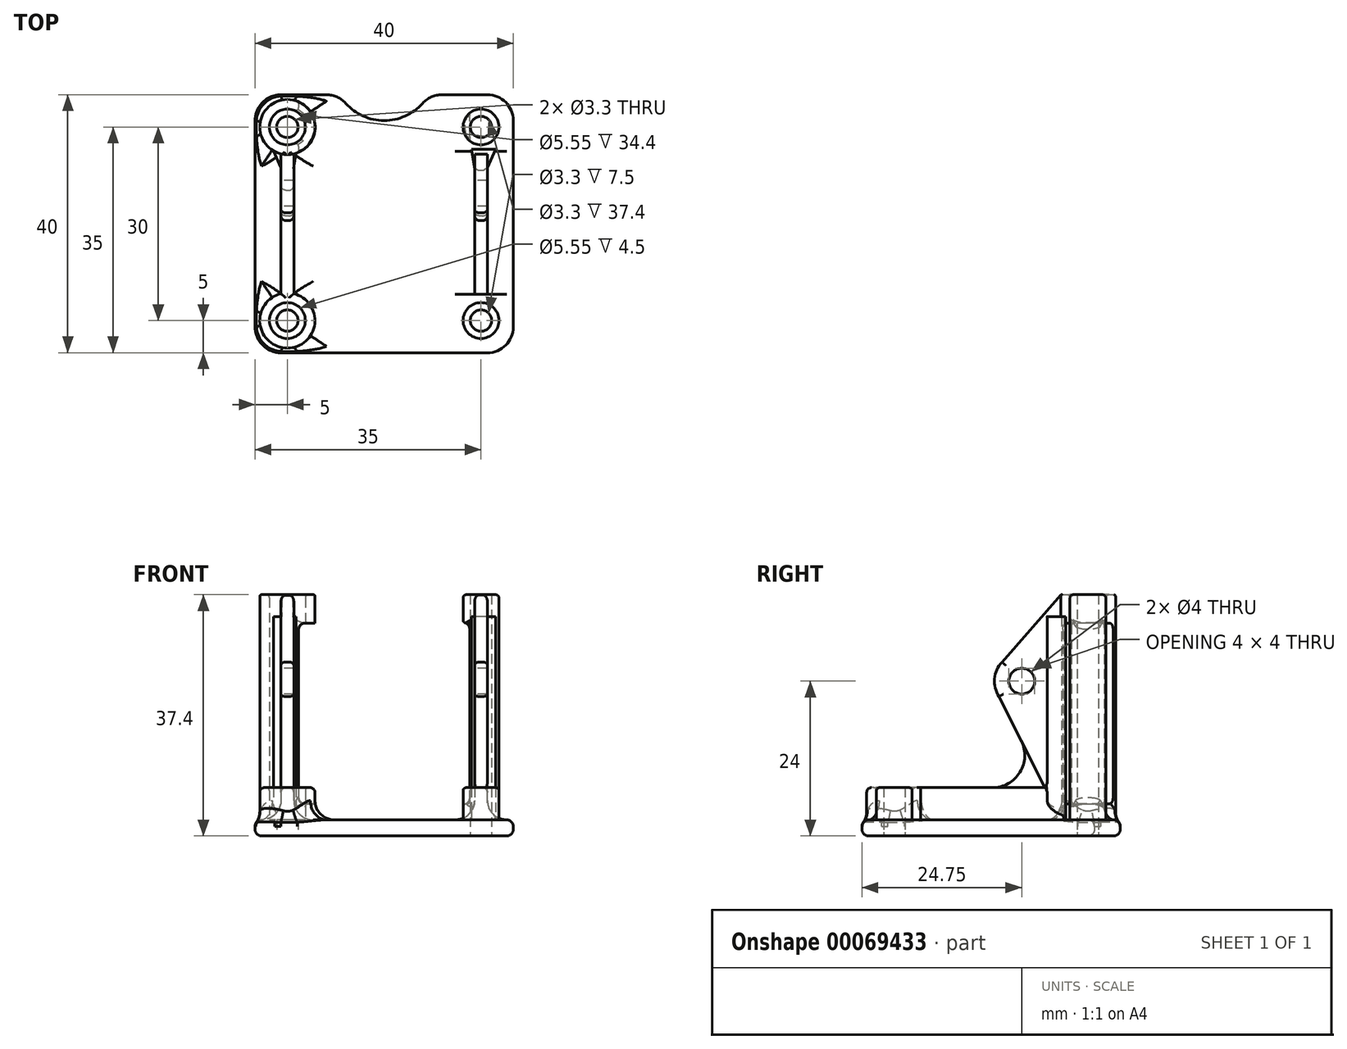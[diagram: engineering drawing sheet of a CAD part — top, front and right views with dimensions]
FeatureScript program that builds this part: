
annotation { "Feature Type Name" : "Feature", "Feature Type Description" : "" }
export const myFeature = defineFeature(function(context is Context, id is Id, definition is map)
    precondition{}
    {
        {
            var Q0;
            Q0=qCreatedBy(makeId("Top.planeOp"),FACE);
            var sketch = newSketch(context, id + "F0", { "sketchPlane" : qUnion([Q0])});
            skLineSegment(sketch, "E0.rect.bottom", {"start": v(20, 20) * mm, "end": v(-20, 20) * mm});
            skLineSegment(sketch, "E0.rect.top", {"start": v(20, -20) * mm, "end": v(-20, -20) * mm});
            skLineSegment(sketch, "E0.rect.left", {"start": v(20, 20) * mm, "end": v(20, -20) * mm});
            skLineSegment(sketch, "E0.rect.right", {"start": v(-20, 20) * mm, "end": v(-20, -20) * mm});
            skPoint(sketch, "E0.rect.middle", {"position": v(0, 0) * mm});
            skCircle(sketch, "E1", {"center": v(-15, 15) * mm, "radius": 1.65 * mm});
            skCircle(sketch, "E2", {"center": v(-15, -15) * mm, "radius": 1.65 * mm});
            skCircle(sketch, "E3.MirrorC", {"center": v(15, 15) * mm, "radius": 1.65 * mm});
            skCircle(sketch, "E4.MirrorC", {"center": v(15, -15) * mm, "radius": 1.65 * mm});
            skCircle(sketch, "E5", {"center": v(0, 24) * mm, "radius": 8 * mm});
            skSolve(sketch);
        }
        {
            var Q0;
            Q0=makeQuery(id+"F0.imprint","IMPRINT",FACE,{"disambiguationData":[TD([[makeQuery(id+"F0.imprint","IMPRINT",EDGE,{"derivedFrom":sQuery(id+"F0.wireOp",EDGE,"E0.rect.top")}),-1.0]])]});
            extrude(context, id + "F1", {"entities" : qUnion([Q0]), "depth" : 2.5 * mm});
        }
        {
            var Q0;
            Q0=makeQuery(id+"F1.opExtrude","CAP_FACE",FACE,{"disambiguationData":[OSD([sQuery(id+"F0.wireOp",EDGE,"E0.rect.bottom"),sQuery(id+"F0.wireOp",EDGE,"E0.rect.top"),sQuery(id+"F0.wireOp",EDGE,"E0.rect.left"),sQuery(id+"F0.wireOp",EDGE,"E0.rect.right"),sQuery(id+"F0.wireOp",EDGE,"E1"),sQuery(id+"F0.wireOp",EDGE,"E2"),sQuery(id+"F0.wireOp",EDGE,"E3.MirrorC"),sQuery(id+"F0.wireOp",EDGE,"E4.MirrorC")])],"isStart":false});
            var sketch = newSketch(context, id + "F2", { "sketchPlane" : qUnion([Q0])});
            skCircle(sketch, "E6", {"center": v(-15, 15) * mm, "radius": 2.77 * mm});
            skCircle(sketch, "E7", {"center": v(-15, 15) * mm, "radius": 4.28 * mm});
            skCircle(sketch, "E8", {"center": v(-15, -15) * mm, "radius": 2.77 * mm});
            skCircle(sketch, "E9", {"center": v(-15, -15) * mm, "radius": 4.28 * mm});
            skCircle(sketch, "E10.MirrorC", {"center": v(15, 15) * mm, "radius": 2.77 * mm});
            skCircle(sketch, "E11.MirrorC", {"center": v(15, 15) * mm, "radius": 4.28 * mm});
            skCircle(sketch, "E12.MirrorC", {"center": v(15, -15) * mm, "radius": 2.77 * mm});
            skCircle(sketch, "E13.MirrorC", {"center": v(15, -15) * mm, "radius": 4.28 * mm});
            skSolve(sketch);
        }
        {
            var Q0;
            Q0=makeQuery(id+"F2.imprint","IMPRINT",FACE,{"disambiguationData":[TD([[makeQuery(id+"F2.imprint","IMPRINT",EDGE,{"derivedFrom":sQuery(id+"F2.wireOp",EDGE,"E8")}),-1.0]])]});
            var Q1;
            Q1=makeQuery(id+"F2.imprint","IMPRINT",FACE,{"disambiguationData":[TD([[makeQuery(id+"F2.imprint","IMPRINT",EDGE,{"derivedFrom":sQuery(id+"F2.wireOp",EDGE,"E12.MirrorC")}),1.0]])]});
            extrude(context, id + "F3", {"entities" : qUnion([Q0, Q1]), "operationType" : NewBodyOperationType.ADD, "depth" : 5 * mm});
        }
        {
            var Q0;
            Q0=makeQuery(id+"F2.imprint","IMPRINT",FACE,{"disambiguationData":[TD([[makeQuery(id+"F2.imprint","IMPRINT",EDGE,{"derivedFrom":sQuery(id+"F2.wireOp",EDGE,"E6")}),-1.0]])]});
            var Q1;
            Q1=makeQuery(id+"F2.imprint","IMPRINT",FACE,{"disambiguationData":[TD([[makeQuery(id+"F2.imprint","IMPRINT",EDGE,{"derivedFrom":sQuery(id+"F2.wireOp",EDGE,"E10.MirrorC")}),1.0]])]});
            extrude(context, id + "F4", {"entities" : qUnion([Q0, Q1]), "operationType" : NewBodyOperationType.ADD, "depth" : 34.9 * mm});
        }
        {
            var Q0;
            Q0=qCreatedBy(makeId("Right.planeOp"),FACE);
            var sketch = newSketch(context, id + "F5", { "sketchPlane" : qUnion([Q0])});
            skLineSegment(sketch, "E14", {"start": v(0, 0) * mm, "end": v(20, 0) * mm});
            skLineSegment(sketch, "E15", {"start": v(20, 0) * mm, "end": v(20, 40) * mm});
            skCircle(sketch, "E16", {"center": v(4.75, 24) * mm, "radius": 4.25 * mm});
            skLineSegment(sketch, "E17", {"start": v(1.23, 21.62) * mm, "end": v(10.81, 2.52) * mm});
            skLineSegment(sketch, "E18", {"start": v(10.81, 2.52) * mm, "end": v(10.81, 37.4) * mm});
            skLineSegment(sketch, "E19", {"start": v(10.81, 37.4) * mm, "end": v(1.7, 26.96) * mm});
            skCircle(sketch, "E20", {"center": v(4.75, 24) * mm, "radius": 2 * mm});
            skSolve(sketch);
        }
        {
            var Q0;
            {var subQ0=sQuery(id+"F5.wireOp",EDGE,"E17");Q0=makeQuery(id+"F5.imprint","IMPRINT",FACE,{"disambiguationData":[TD([[makeQuery(id+"F5.imprint","IMPRINT",EDGE,{"derivedFrom":subQ0}),1.0]])]});}
            var Q1;
            Q1=makeQuery(id+"F5.imprint","IMPRINT",FACE,{"disambiguationData":[TD([[makeQuery(id+"F5.imprint","IMPRINT",EDGE,{"derivedFrom":sQuery(id+"F5.wireOp",EDGE,"E20")}),-1.0]])]});
            extrude(context, id + "F6", {"entities" : qUnion([Q0, Q1]), "operationType" : NewBodyOperationType.ADD, "endBound" : BoundingType.SYMMETRIC, "depth" : 32 * mm});
        }
        {
            var Q0;
            Q0=qCreatedBy(makeId("Front.planeOp"),FACE);
            var sketch = newSketch(context, id + "F7", { "sketchPlane" : qUnion([Q0])});
            skLineSegment(sketch, "E21.rect.bottom", {"start": v(-14, 37.5) * mm, "end": v(14, 37.5) * mm});
            skLineSegment(sketch, "E21.rect.top", {"start": v(-14, 2.5) * mm, "end": v(14, 2.5) * mm});
            skLineSegment(sketch, "E21.rect.left", {"start": v(-14, 37.5) * mm, "end": v(-14, 2.5) * mm});
            skLineSegment(sketch, "E21.rect.right", {"start": v(14, 37.5) * mm, "end": v(14, 2.5) * mm});
            skPoint(sketch, "E21.rect.middle", {"position": v(0, 20) * mm});
            skSolve(sketch);
        }
        {
            var Q0;
            Q0=makeQuery(id+"F7.imprint","IMPRINT",FACE,{"disambiguationData":[TD([[makeQuery(id+"F7.imprint","IMPRINT",EDGE,{"derivedFrom":sQuery(id+"F7.wireOp",EDGE,"E21.rect.bottom")}),-1.0]])]});
            var Q1;
            Q1=makeQuery(id+"F6.opExtrude","SWEPT_FACE",FACE,{"disambiguationData":[OSD([sQuery(id+"F5.wireOp",EDGE,"E18")])]});
            extrude(context, id + "F8", {"entities" : qUnion([Q0]), "operationType" : NewBodyOperationType.REMOVE, "endBound" : BoundingType.UP_TO_SURFACE, "oppositeDirection" : true, "endBoundEntityFace" : qUnion([Q1]), "depth" : 25 * mm});
        }
        {
            var Q0;
            Q0=qCreatedBy(makeId("Front.planeOp"),FACE);
            var sketch = newSketch(context, id + "F9", { "sketchPlane" : qUnion([Q0])});
            skLineSegment(sketch, "E22.rect.bottom", {"start": v(-13.25, 33) * mm, "end": v(13.25, 33) * mm});
            skLineSegment(sketch, "E22.rect.top", {"start": v(-13.25, 5) * mm, "end": v(13.25, 5) * mm});
            skLineSegment(sketch, "E22.rect.left", {"start": v(-13.25, 33) * mm, "end": v(-13.25, 5) * mm});
            skLineSegment(sketch, "E22.rect.right", {"start": v(13.25, 33) * mm, "end": v(13.25, 5) * mm});
            skPoint(sketch, "E22.rect.middle", {"position": v(0, 19) * mm});
            skSolve(sketch);
        }
        {
            var Q0;
            Q0=makeQuery(id+"F9.imprint","IMPRINT",FACE,{"disambiguationData":[TD([[makeQuery(id+"F9.imprint","IMPRINT",EDGE,{"derivedFrom":sQuery(id+"F9.wireOp",EDGE,"E22.rect.bottom")}),-1.0]])]});
            extrude(context, id + "F10", {"entities" : qUnion([Q0]), "operationType" : NewBodyOperationType.REMOVE, "oppositeDirection" : true, "depth" : 25 * mm});
        }
        {
            var Q0;
            Q0=qCreatedBy(makeId("Top.planeOp"),FACE);
            var sketch = newSketch(context, id + "F11", { "sketchPlane" : qUnion([Q0])});
            skLineSegment(sketch, "E23", {"start": v(-14, 11.25) * mm, "end": v(-14, -10.94) * mm});
            skLineSegment(sketch, "E24", {"start": v(-14, -10.94) * mm, "end": v(-16, -10.94) * mm});
            skLineSegment(sketch, "E25", {"start": v(-16, -10.94) * mm, "end": v(-16, 11.25) * mm});
            skLineSegment(sketch, "E26", {"start": v(-16, 11.25) * mm, "end": v(-14, 11.25) * mm});
            skLineSegment(sketch, "E27.MirrorCS", {"start": v(16, 11.25) * mm, "end": v(14, 11.25) * mm});
            skLineSegment(sketch, "E28.MirrorCS", {"start": v(14, -10.94) * mm, "end": v(16, -10.94) * mm});
            skLineSegment(sketch, "E29.MirrorCS", {"start": v(16, -10.94) * mm, "end": v(16, 11.25) * mm});
            skLineSegment(sketch, "E30.MirrorCS", {"start": v(14, 11.25) * mm, "end": v(14, -10.94) * mm});
            skSolve(sketch);
        }
        {
            var Q0;
            Q0 = qSketchRegion(id + "F11", true);
            extrude(context, id + "F12", {"entities" : qUnion([Q0]), "operationType" : NewBodyOperationType.ADD, "depth" : 7.5 * mm});
        }
        {
            var Q0;
            Q0=makeQuery(id+"F1.opExtrude","SWEPT_EDGE",EDGE,{"disambiguationData":[OSD([sQuery(id+"F0.wireOp",EDGE,"E0.rect.top"),sQuery(id+"F0.wireOp",EDGE,"E0.rect.left")])]});
            var Q1;
            Q1=makeQuery(id+"F1.opExtrude","SWEPT_EDGE",EDGE,{"disambiguationData":[OSD([sQuery(id+"F0.wireOp",EDGE,"E0.rect.top"),sQuery(id+"F0.wireOp",EDGE,"E0.rect.right")])]});
            var Q2;
            Q2=makeQuery(id+"F1.opExtrude","SWEPT_EDGE",EDGE,{"disambiguationData":[OSD([sQuery(id+"F0.wireOp",EDGE,"E0.rect.bottom"),sQuery(id+"F0.wireOp",EDGE,"E0.rect.right")])]});
            var Q3;
            Q3=makeQuery(id+"F1.opExtrude","SWEPT_EDGE",EDGE,{"disambiguationData":[OSD([sQuery(id+"F0.wireOp",EDGE,"E0.rect.bottom"),sQuery(id+"F0.wireOp",EDGE,"E0.rect.left")])]});
            var Q4;
            {var subQ0=sQuery(id+"F0.wireOp",EDGE,"E5");var subQ1=sQuery(id+"F0.wireOp",EDGE,"E0.rect.bottom");Q4=makeQuery(id+"F1.opExtrude","SWEPT_EDGE",EDGE,{"disambiguationData":[OSD([subQ1,subQ0]),TDD([makeQuery(id+"F0.imprint","INTERSECT",VERTEX,{"disambiguationData":[OD(0.0)],"derivedFrom":[subQ1,subQ0]})])]});}
            var Q5;
            {var subQ0=sQuery(id+"F0.wireOp",EDGE,"E5");var subQ1=sQuery(id+"F0.wireOp",EDGE,"E0.rect.bottom");Q5=makeQuery(id+"F1.opExtrude","SWEPT_EDGE",EDGE,{"disambiguationData":[OSD([subQ1,subQ0]),TDD([makeQuery(id+"F0.imprint","INTERSECT",VERTEX,{"disambiguationData":[OD(1.0)],"derivedFrom":[subQ1,subQ0]})])]});}
            fillet(context, id + "F13", {"entities" : qUnion([Q0, Q1, Q2, Q3, Q4, Q5]), "radius" : 4 * mm, "tangentPropagation" : true, "allowEdgeOverflow" : false});
        }
        {
            var Q0;
            Q0=makeQuery(id+"F1.opExtrude","CAP_EDGE",EDGE,{"disambiguationData":[OSD([sQuery(id+"F0.wireOp",EDGE,"E0.rect.right")])],"isStart":false});
            var Q1;
            Q1=makeQuery(id+"F1.opExtrude","CAP_EDGE",EDGE,{"disambiguationData":[OSD([sQuery(id+"F0.wireOp",EDGE,"E0.rect.right")])],"isStart":true});
            var Q2;
            {var subQ0=sQuery(id+"F0.wireOp",EDGE,"E0.rect.right");var subQ1=sQuery(id+"F0.wireOp",EDGE,"E0.rect.top");Q2=makeQuery(id+"F13.opFillet","BLEND_EDGE",EDGE,{"blendedFrom":[makeQuery(id+"F1.opExtrude","SWEPT_EDGE",EDGE,{"disambiguationData":[OSD([subQ1,subQ0])]}),makeQuery(id+"F1.opExtrude","CAP_FACE",FACE,{"disambiguationData":[OSD([sQuery(id+"F0.wireOp",EDGE,"E0.rect.bottom"),subQ1,sQuery(id+"F0.wireOp",EDGE,"E0.rect.left"),subQ0,sQuery(id+"F0.wireOp",EDGE,"E1"),sQuery(id+"F0.wireOp",EDGE,"E2"),sQuery(id+"F0.wireOp",EDGE,"E3.MirrorC"),sQuery(id+"F0.wireOp",EDGE,"E4.MirrorC"),sQuery(id+"F0.wireOp",EDGE,"E5")])],"isStart":true})],"blendedInto":[makeQuery(id+"F1.opExtrude","CAP_FACE",FACE,{"disambiguationData":[OSD([sQuery(id+"F0.wireOp",EDGE,"E0.rect.bottom"),subQ1,sQuery(id+"F0.wireOp",EDGE,"E0.rect.left"),subQ0,sQuery(id+"F0.wireOp",EDGE,"E1"),sQuery(id+"F0.wireOp",EDGE,"E2"),sQuery(id+"F0.wireOp",EDGE,"E3.MirrorC"),sQuery(id+"F0.wireOp",EDGE,"E4.MirrorC"),sQuery(id+"F0.wireOp",EDGE,"E5")])],"isStart":true})]});}
            var Q3;
            {var subQ0=sQuery(id+"F0.wireOp",EDGE,"E0.rect.left");var subQ2=sQuery(id+"F0.wireOp",EDGE,"E0.rect.top");var subQ3=makeQuery(id+"F1.opExtrude","SWEPT_FACE",FACE,{"disambiguationData":[OSD([subQ2])]});var subQ4=sQuery(id+"F0.wireOp",EDGE,"E0.rect.right");var subQ5=sQuery(id+"F0.wireOp",EDGE,"E0.rect.bottom");var subQ6=sQuery(id+"F0.wireOp",EDGE,"E5");var subQ13=sQuery(id+"F0.wireOp",EDGE,"E1");var subQ14=sQuery(id+"F0.wireOp",EDGE,"E3.MirrorC");Q3=makeQuery(id+"F13.opFillet","BLEND_EDGE",EDGE,{"blendedFrom":[makeQuery(id+"F1.opExtrude","SWEPT_EDGE",EDGE,{"disambiguationData":[OSD([subQ2,subQ4])]}),makeQuery(id+"F4.boolean.opBoolean","SPLIT",FACE,{"disambiguationData":[TD([subQ3])],"derivedFrom":makeQuery(id+"F3.boolean.opBoolean","SPLIT",FACE,{"disambiguationData":[TD([subQ3])],"derivedFrom":makeQuery(id+"F1.opExtrude","CAP_FACE",FACE,{"disambiguationData":[OSD([subQ5,subQ2,subQ0,subQ4,subQ13,sQuery(id+"F0.wireOp",EDGE,"E2"),subQ14,sQuery(id+"F0.wireOp",EDGE,"E4.MirrorC"),subQ6])],"isStart":false})})})],"blendedInto":[makeQuery(id+"F4.boolean.opBoolean","SPLIT",FACE,{"disambiguationData":[TD([subQ3])],"derivedFrom":makeQuery(id+"F3.boolean.opBoolean","SPLIT",FACE,{"disambiguationData":[TD([subQ3])],"derivedFrom":makeQuery(id+"F1.opExtrude","CAP_FACE",FACE,{"disambiguationData":[OSD([subQ5,subQ2,subQ0,subQ4,subQ13,sQuery(id+"F0.wireOp",EDGE,"E2"),subQ14,sQuery(id+"F0.wireOp",EDGE,"E4.MirrorC"),subQ6])],"isStart":false})})})]});}
            var Q4;
            Q4=makeQuery(id+"F1.opExtrude","CAP_EDGE",EDGE,{"disambiguationData":[OSD([sQuery(id+"F0.wireOp",EDGE,"E0.rect.top")])],"isStart":false});
            var Q5;
            Q5=makeQuery(id+"F1.opExtrude","CAP_EDGE",EDGE,{"disambiguationData":[OSD([sQuery(id+"F0.wireOp",EDGE,"E0.rect.top")])],"isStart":true});
            var Q6;
            {var subQ0=sQuery(id+"F0.wireOp",EDGE,"E0.rect.left");var subQ2=sQuery(id+"F0.wireOp",EDGE,"E0.rect.top");var subQ3=makeQuery(id+"F1.opExtrude","SWEPT_FACE",FACE,{"disambiguationData":[OSD([subQ2])]});var subQ4=sQuery(id+"F0.wireOp",EDGE,"E0.rect.right");var subQ5=sQuery(id+"F0.wireOp",EDGE,"E0.rect.bottom");var subQ6=sQuery(id+"F0.wireOp",EDGE,"E5");var subQ13=sQuery(id+"F0.wireOp",EDGE,"E1");var subQ14=sQuery(id+"F0.wireOp",EDGE,"E3.MirrorC");Q6=makeQuery(id+"F13.opFillet","BLEND_EDGE",EDGE,{"blendedFrom":[makeQuery(id+"F1.opExtrude","SWEPT_EDGE",EDGE,{"disambiguationData":[OSD([subQ2,subQ0])]}),makeQuery(id+"F4.boolean.opBoolean","SPLIT",FACE,{"disambiguationData":[TD([subQ3])],"derivedFrom":makeQuery(id+"F3.boolean.opBoolean","SPLIT",FACE,{"disambiguationData":[TD([subQ3])],"derivedFrom":makeQuery(id+"F1.opExtrude","CAP_FACE",FACE,{"disambiguationData":[OSD([subQ5,subQ2,subQ0,subQ4,subQ13,sQuery(id+"F0.wireOp",EDGE,"E2"),subQ14,sQuery(id+"F0.wireOp",EDGE,"E4.MirrorC"),subQ6])],"isStart":false})})})],"blendedInto":[makeQuery(id+"F4.boolean.opBoolean","SPLIT",FACE,{"disambiguationData":[TD([subQ3])],"derivedFrom":makeQuery(id+"F3.boolean.opBoolean","SPLIT",FACE,{"disambiguationData":[TD([subQ3])],"derivedFrom":makeQuery(id+"F1.opExtrude","CAP_FACE",FACE,{"disambiguationData":[OSD([subQ5,subQ2,subQ0,subQ4,subQ13,sQuery(id+"F0.wireOp",EDGE,"E2"),subQ14,sQuery(id+"F0.wireOp",EDGE,"E4.MirrorC"),subQ6])],"isStart":false})})})]});}
            var Q7;
            {var subQ0=sQuery(id+"F0.wireOp",EDGE,"E0.rect.left");var subQ1=sQuery(id+"F0.wireOp",EDGE,"E0.rect.top");Q7=makeQuery(id+"F13.opFillet","BLEND_EDGE",EDGE,{"blendedFrom":[makeQuery(id+"F1.opExtrude","SWEPT_EDGE",EDGE,{"disambiguationData":[OSD([subQ1,subQ0])]}),makeQuery(id+"F1.opExtrude","CAP_FACE",FACE,{"disambiguationData":[OSD([sQuery(id+"F0.wireOp",EDGE,"E0.rect.bottom"),subQ1,subQ0,sQuery(id+"F0.wireOp",EDGE,"E0.rect.right"),sQuery(id+"F0.wireOp",EDGE,"E1"),sQuery(id+"F0.wireOp",EDGE,"E2"),sQuery(id+"F0.wireOp",EDGE,"E3.MirrorC"),sQuery(id+"F0.wireOp",EDGE,"E4.MirrorC"),sQuery(id+"F0.wireOp",EDGE,"E5")])],"isStart":true})],"blendedInto":[makeQuery(id+"F1.opExtrude","CAP_FACE",FACE,{"disambiguationData":[OSD([sQuery(id+"F0.wireOp",EDGE,"E0.rect.bottom"),subQ1,subQ0,sQuery(id+"F0.wireOp",EDGE,"E0.rect.right"),sQuery(id+"F0.wireOp",EDGE,"E1"),sQuery(id+"F0.wireOp",EDGE,"E2"),sQuery(id+"F0.wireOp",EDGE,"E3.MirrorC"),sQuery(id+"F0.wireOp",EDGE,"E4.MirrorC"),sQuery(id+"F0.wireOp",EDGE,"E5")])],"isStart":true})]});}
            var Q8;
            Q8=makeQuery(id+"F1.opExtrude","CAP_EDGE",EDGE,{"disambiguationData":[OSD([sQuery(id+"F0.wireOp",EDGE,"E0.rect.left")])],"isStart":true});
            var Q9;
            Q9=makeQuery(id+"F1.opExtrude","CAP_EDGE",EDGE,{"disambiguationData":[OSD([sQuery(id+"F0.wireOp",EDGE,"E0.rect.left")])],"isStart":false});
            var Q10;
            {var subQ0=sQuery(id+"F0.wireOp",EDGE,"E0.rect.left");var subQ2=sQuery(id+"F0.wireOp",EDGE,"E0.rect.top");var subQ3=makeQuery(id+"F1.opExtrude","SWEPT_FACE",FACE,{"disambiguationData":[OSD([subQ2])]});var subQ4=sQuery(id+"F0.wireOp",EDGE,"E0.rect.right");var subQ5=sQuery(id+"F0.wireOp",EDGE,"E0.rect.bottom");var subQ6=sQuery(id+"F0.wireOp",EDGE,"E5");var subQ13=sQuery(id+"F0.wireOp",EDGE,"E1");var subQ14=sQuery(id+"F0.wireOp",EDGE,"E3.MirrorC");Q10=makeQuery(id+"F13.opFillet","BLEND_EDGE",EDGE,{"blendedFrom":[makeQuery(id+"F1.opExtrude","SWEPT_EDGE",EDGE,{"disambiguationData":[OSD([subQ5,subQ0])]}),makeQuery(id+"F4.boolean.opBoolean","SPLIT",FACE,{"disambiguationData":[TD([subQ3])],"derivedFrom":makeQuery(id+"F3.boolean.opBoolean","SPLIT",FACE,{"disambiguationData":[TD([subQ3])],"derivedFrom":makeQuery(id+"F1.opExtrude","CAP_FACE",FACE,{"disambiguationData":[OSD([subQ5,subQ2,subQ0,subQ4,subQ13,sQuery(id+"F0.wireOp",EDGE,"E2"),subQ14,sQuery(id+"F0.wireOp",EDGE,"E4.MirrorC"),subQ6])],"isStart":false})})})],"blendedInto":[makeQuery(id+"F4.boolean.opBoolean","SPLIT",FACE,{"disambiguationData":[TD([subQ3])],"derivedFrom":makeQuery(id+"F3.boolean.opBoolean","SPLIT",FACE,{"disambiguationData":[TD([subQ3])],"derivedFrom":makeQuery(id+"F1.opExtrude","CAP_FACE",FACE,{"disambiguationData":[OSD([subQ5,subQ2,subQ0,subQ4,subQ13,sQuery(id+"F0.wireOp",EDGE,"E2"),subQ14,sQuery(id+"F0.wireOp",EDGE,"E4.MirrorC"),subQ6])],"isStart":false})})})]});}
            var Q11;
            {var subQ0=sQuery(id+"F0.wireOp",EDGE,"E0.rect.left");var subQ1=sQuery(id+"F0.wireOp",EDGE,"E0.rect.bottom");Q11=makeQuery(id+"F13.opFillet","BLEND_EDGE",EDGE,{"blendedFrom":[makeQuery(id+"F1.opExtrude","SWEPT_EDGE",EDGE,{"disambiguationData":[OSD([subQ1,subQ0])]}),makeQuery(id+"F1.opExtrude","CAP_FACE",FACE,{"disambiguationData":[OSD([subQ1,sQuery(id+"F0.wireOp",EDGE,"E0.rect.top"),subQ0,sQuery(id+"F0.wireOp",EDGE,"E0.rect.right"),sQuery(id+"F0.wireOp",EDGE,"E1"),sQuery(id+"F0.wireOp",EDGE,"E2"),sQuery(id+"F0.wireOp",EDGE,"E3.MirrorC"),sQuery(id+"F0.wireOp",EDGE,"E4.MirrorC"),sQuery(id+"F0.wireOp",EDGE,"E5")])],"isStart":true})],"blendedInto":[makeQuery(id+"F1.opExtrude","CAP_FACE",FACE,{"disambiguationData":[OSD([subQ1,sQuery(id+"F0.wireOp",EDGE,"E0.rect.top"),subQ0,sQuery(id+"F0.wireOp",EDGE,"E0.rect.right"),sQuery(id+"F0.wireOp",EDGE,"E1"),sQuery(id+"F0.wireOp",EDGE,"E2"),sQuery(id+"F0.wireOp",EDGE,"E3.MirrorC"),sQuery(id+"F0.wireOp",EDGE,"E4.MirrorC"),sQuery(id+"F0.wireOp",EDGE,"E5")])],"isStart":true})]});}
            var Q12;
            {var subQ0=sQuery(id+"F0.wireOp",EDGE,"E0.rect.bottom");Q12=makeQuery(id+"F1.opExtrude","CAP_EDGE",EDGE,{"disambiguationData":[OSD([subQ0]),TDD([makeQuery(id+"F0.imprint","IMPRINT",EDGE,{"disambiguationData":[TD([[makeQuery(id+"F0.imprint","INTERSECT",VERTEX,{"derivedFrom":[subQ0,sQuery(id+"F0.wireOp",EDGE,"E0.rect.left")]}),-1.0]])],"derivedFrom":subQ0})])],"isStart":true});}
            var Q13;
            {var subQ0=sQuery(id+"F0.wireOp",EDGE,"E0.rect.bottom");Q13=makeQuery(id+"F1.opExtrude","CAP_EDGE",EDGE,{"disambiguationData":[OSD([subQ0]),TDD([makeQuery(id+"F0.imprint","IMPRINT",EDGE,{"disambiguationData":[TD([[makeQuery(id+"F0.imprint","INTERSECT",VERTEX,{"derivedFrom":[subQ0,sQuery(id+"F0.wireOp",EDGE,"E0.rect.left")]}),-1.0]])],"derivedFrom":subQ0})])],"isStart":false});}
            var Q14;
            {var subQ0=sQuery(id+"F0.wireOp",EDGE,"E0.rect.left");var subQ2=sQuery(id+"F0.wireOp",EDGE,"E0.rect.top");var subQ3=makeQuery(id+"F1.opExtrude","SWEPT_FACE",FACE,{"disambiguationData":[OSD([subQ2])]});var subQ4=sQuery(id+"F0.wireOp",EDGE,"E0.rect.right");var subQ5=sQuery(id+"F0.wireOp",EDGE,"E0.rect.bottom");var subQ6=sQuery(id+"F0.wireOp",EDGE,"E5");var subQ8=makeQuery(id+"F0.imprint","INTERSECT",VERTEX,{"disambiguationData":[OD(0.0)],"derivedFrom":[subQ5,subQ6]});var subQ14=sQuery(id+"F0.wireOp",EDGE,"E1");var subQ15=sQuery(id+"F0.wireOp",EDGE,"E3.MirrorC");Q14=makeQuery(id+"F13.opFillet","BLEND_EDGE",EDGE,{"blendedFrom":[makeQuery(id+"F1.opExtrude","SWEPT_EDGE",EDGE,{"disambiguationData":[OSD([subQ5,subQ6]),TDD([subQ8])]}),makeQuery(id+"F4.boolean.opBoolean","SPLIT",FACE,{"disambiguationData":[TD([subQ3])],"derivedFrom":makeQuery(id+"F3.boolean.opBoolean","SPLIT",FACE,{"disambiguationData":[TD([subQ3])],"derivedFrom":makeQuery(id+"F1.opExtrude","CAP_FACE",FACE,{"disambiguationData":[OSD([subQ5,subQ2,subQ0,subQ4,subQ14,sQuery(id+"F0.wireOp",EDGE,"E2"),subQ15,sQuery(id+"F0.wireOp",EDGE,"E4.MirrorC"),subQ6])],"isStart":false})})})],"blendedInto":[makeQuery(id+"F4.boolean.opBoolean","SPLIT",FACE,{"disambiguationData":[TD([subQ3])],"derivedFrom":makeQuery(id+"F3.boolean.opBoolean","SPLIT",FACE,{"disambiguationData":[TD([subQ3])],"derivedFrom":makeQuery(id+"F1.opExtrude","CAP_FACE",FACE,{"disambiguationData":[OSD([subQ5,subQ2,subQ0,subQ4,subQ14,sQuery(id+"F0.wireOp",EDGE,"E2"),subQ15,sQuery(id+"F0.wireOp",EDGE,"E4.MirrorC"),subQ6])],"isStart":false})})})]});}
            var Q15;
            Q15=makeQuery(id+"F1.opExtrude","CAP_EDGE",EDGE,{"disambiguationData":[OSD([sQuery(id+"F0.wireOp",EDGE,"E5")])],"isStart":true});
            var Q16;
            {var subQ0=sQuery(id+"F0.wireOp",EDGE,"E5");var subQ1=sQuery(id+"F0.wireOp",EDGE,"E0.rect.bottom");Q16=makeQuery(id+"F13.opFillet","BLEND_EDGE",EDGE,{"blendedFrom":[makeQuery(id+"F1.opExtrude","SWEPT_EDGE",EDGE,{"disambiguationData":[OSD([subQ1,subQ0]),TDD([makeQuery(id+"F0.imprint","INTERSECT",VERTEX,{"disambiguationData":[OD(0.0)],"derivedFrom":[subQ1,subQ0]})])]}),makeQuery(id+"F1.opExtrude","CAP_FACE",FACE,{"disambiguationData":[OSD([subQ1,sQuery(id+"F0.wireOp",EDGE,"E0.rect.top"),sQuery(id+"F0.wireOp",EDGE,"E0.rect.left"),sQuery(id+"F0.wireOp",EDGE,"E0.rect.right"),sQuery(id+"F0.wireOp",EDGE,"E1"),sQuery(id+"F0.wireOp",EDGE,"E2"),sQuery(id+"F0.wireOp",EDGE,"E3.MirrorC"),sQuery(id+"F0.wireOp",EDGE,"E4.MirrorC"),subQ0])],"isStart":true})],"blendedInto":[makeQuery(id+"F1.opExtrude","CAP_FACE",FACE,{"disambiguationData":[OSD([subQ1,sQuery(id+"F0.wireOp",EDGE,"E0.rect.top"),sQuery(id+"F0.wireOp",EDGE,"E0.rect.left"),sQuery(id+"F0.wireOp",EDGE,"E0.rect.right"),sQuery(id+"F0.wireOp",EDGE,"E1"),sQuery(id+"F0.wireOp",EDGE,"E2"),sQuery(id+"F0.wireOp",EDGE,"E3.MirrorC"),sQuery(id+"F0.wireOp",EDGE,"E4.MirrorC"),subQ0])],"isStart":true})]});}
            var Q17;
            Q17=makeQuery(id+"F1.opExtrude","CAP_EDGE",EDGE,{"disambiguationData":[OSD([sQuery(id+"F0.wireOp",EDGE,"E5")])],"isStart":false});
            var Q18;
            {var subQ0=sQuery(id+"F0.wireOp",EDGE,"E0.rect.left");var subQ2=sQuery(id+"F0.wireOp",EDGE,"E0.rect.top");var subQ3=makeQuery(id+"F1.opExtrude","SWEPT_FACE",FACE,{"disambiguationData":[OSD([subQ2])]});var subQ4=sQuery(id+"F0.wireOp",EDGE,"E0.rect.right");var subQ5=sQuery(id+"F0.wireOp",EDGE,"E0.rect.bottom");var subQ6=sQuery(id+"F0.wireOp",EDGE,"E5");var subQ7=makeQuery(id+"F0.imprint","INTERSECT",VERTEX,{"disambiguationData":[OD(1.0)],"derivedFrom":[subQ5,subQ6]});var subQ14=sQuery(id+"F0.wireOp",EDGE,"E1");var subQ15=sQuery(id+"F0.wireOp",EDGE,"E3.MirrorC");Q18=makeQuery(id+"F13.opFillet","BLEND_EDGE",EDGE,{"blendedFrom":[makeQuery(id+"F1.opExtrude","SWEPT_EDGE",EDGE,{"disambiguationData":[OSD([subQ5,subQ6]),TDD([subQ7])]}),makeQuery(id+"F4.boolean.opBoolean","SPLIT",FACE,{"disambiguationData":[TD([subQ3])],"derivedFrom":makeQuery(id+"F3.boolean.opBoolean","SPLIT",FACE,{"disambiguationData":[TD([subQ3])],"derivedFrom":makeQuery(id+"F1.opExtrude","CAP_FACE",FACE,{"disambiguationData":[OSD([subQ5,subQ2,subQ0,subQ4,subQ14,sQuery(id+"F0.wireOp",EDGE,"E2"),subQ15,sQuery(id+"F0.wireOp",EDGE,"E4.MirrorC"),subQ6])],"isStart":false})})})],"blendedInto":[makeQuery(id+"F4.boolean.opBoolean","SPLIT",FACE,{"disambiguationData":[TD([subQ3])],"derivedFrom":makeQuery(id+"F3.boolean.opBoolean","SPLIT",FACE,{"disambiguationData":[TD([subQ3])],"derivedFrom":makeQuery(id+"F1.opExtrude","CAP_FACE",FACE,{"disambiguationData":[OSD([subQ5,subQ2,subQ0,subQ4,subQ14,sQuery(id+"F0.wireOp",EDGE,"E2"),subQ15,sQuery(id+"F0.wireOp",EDGE,"E4.MirrorC"),subQ6])],"isStart":false})})})]});}
            var Q19;
            {var subQ0=sQuery(id+"F0.wireOp",EDGE,"E5");var subQ1=sQuery(id+"F0.wireOp",EDGE,"E0.rect.bottom");Q19=makeQuery(id+"F13.opFillet","BLEND_EDGE",EDGE,{"blendedFrom":[makeQuery(id+"F1.opExtrude","SWEPT_EDGE",EDGE,{"disambiguationData":[OSD([subQ1,subQ0]),TDD([makeQuery(id+"F0.imprint","INTERSECT",VERTEX,{"disambiguationData":[OD(1.0)],"derivedFrom":[subQ1,subQ0]})])]}),makeQuery(id+"F1.opExtrude","CAP_FACE",FACE,{"disambiguationData":[OSD([subQ1,sQuery(id+"F0.wireOp",EDGE,"E0.rect.top"),sQuery(id+"F0.wireOp",EDGE,"E0.rect.left"),sQuery(id+"F0.wireOp",EDGE,"E0.rect.right"),sQuery(id+"F0.wireOp",EDGE,"E1"),sQuery(id+"F0.wireOp",EDGE,"E2"),sQuery(id+"F0.wireOp",EDGE,"E3.MirrorC"),sQuery(id+"F0.wireOp",EDGE,"E4.MirrorC"),subQ0])],"isStart":true})],"blendedInto":[makeQuery(id+"F1.opExtrude","CAP_FACE",FACE,{"disambiguationData":[OSD([subQ1,sQuery(id+"F0.wireOp",EDGE,"E0.rect.top"),sQuery(id+"F0.wireOp",EDGE,"E0.rect.left"),sQuery(id+"F0.wireOp",EDGE,"E0.rect.right"),sQuery(id+"F0.wireOp",EDGE,"E1"),sQuery(id+"F0.wireOp",EDGE,"E2"),sQuery(id+"F0.wireOp",EDGE,"E3.MirrorC"),sQuery(id+"F0.wireOp",EDGE,"E4.MirrorC"),subQ0])],"isStart":true})]});}
            var Q20;
            {var subQ0=sQuery(id+"F0.wireOp",EDGE,"E0.rect.bottom");Q20=makeQuery(id+"F1.opExtrude","CAP_EDGE",EDGE,{"disambiguationData":[OSD([subQ0]),TDD([makeQuery(id+"F0.imprint","IMPRINT",EDGE,{"disambiguationData":[TD([[makeQuery(id+"F0.imprint","INTERSECT",VERTEX,{"derivedFrom":[subQ0,sQuery(id+"F0.wireOp",EDGE,"E0.rect.right")]}),1.0]])],"derivedFrom":subQ0})])],"isStart":false});}
            var Q21;
            {var subQ0=sQuery(id+"F0.wireOp",EDGE,"E0.rect.bottom");Q21=makeQuery(id+"F1.opExtrude","CAP_EDGE",EDGE,{"disambiguationData":[OSD([subQ0]),TDD([makeQuery(id+"F0.imprint","IMPRINT",EDGE,{"disambiguationData":[TD([[makeQuery(id+"F0.imprint","INTERSECT",VERTEX,{"derivedFrom":[subQ0,sQuery(id+"F0.wireOp",EDGE,"E0.rect.right")]}),1.0]])],"derivedFrom":subQ0})])],"isStart":true});}
            var Q22;
            {var subQ0=sQuery(id+"F0.wireOp",EDGE,"E0.rect.right");var subQ1=sQuery(id+"F0.wireOp",EDGE,"E0.rect.bottom");Q22=makeQuery(id+"F13.opFillet","BLEND_EDGE",EDGE,{"blendedFrom":[makeQuery(id+"F1.opExtrude","SWEPT_EDGE",EDGE,{"disambiguationData":[OSD([subQ1,subQ0])]}),makeQuery(id+"F1.opExtrude","CAP_FACE",FACE,{"disambiguationData":[OSD([subQ1,sQuery(id+"F0.wireOp",EDGE,"E0.rect.top"),sQuery(id+"F0.wireOp",EDGE,"E0.rect.left"),subQ0,sQuery(id+"F0.wireOp",EDGE,"E1"),sQuery(id+"F0.wireOp",EDGE,"E2"),sQuery(id+"F0.wireOp",EDGE,"E3.MirrorC"),sQuery(id+"F0.wireOp",EDGE,"E4.MirrorC"),sQuery(id+"F0.wireOp",EDGE,"E5")])],"isStart":true})],"blendedInto":[makeQuery(id+"F1.opExtrude","CAP_FACE",FACE,{"disambiguationData":[OSD([subQ1,sQuery(id+"F0.wireOp",EDGE,"E0.rect.top"),sQuery(id+"F0.wireOp",EDGE,"E0.rect.left"),subQ0,sQuery(id+"F0.wireOp",EDGE,"E1"),sQuery(id+"F0.wireOp",EDGE,"E2"),sQuery(id+"F0.wireOp",EDGE,"E3.MirrorC"),sQuery(id+"F0.wireOp",EDGE,"E4.MirrorC"),sQuery(id+"F0.wireOp",EDGE,"E5")])],"isStart":true})]});}
            var Q23;
            {var subQ0=sQuery(id+"F0.wireOp",EDGE,"E0.rect.left");var subQ2=sQuery(id+"F0.wireOp",EDGE,"E0.rect.top");var subQ3=makeQuery(id+"F1.opExtrude","SWEPT_FACE",FACE,{"disambiguationData":[OSD([subQ2])]});var subQ4=sQuery(id+"F0.wireOp",EDGE,"E0.rect.right");var subQ5=sQuery(id+"F0.wireOp",EDGE,"E0.rect.bottom");var subQ6=sQuery(id+"F0.wireOp",EDGE,"E5");var subQ13=sQuery(id+"F0.wireOp",EDGE,"E1");var subQ14=sQuery(id+"F0.wireOp",EDGE,"E3.MirrorC");Q23=makeQuery(id+"F13.opFillet","BLEND_EDGE",EDGE,{"blendedFrom":[makeQuery(id+"F1.opExtrude","SWEPT_EDGE",EDGE,{"disambiguationData":[OSD([subQ5,subQ4])]}),makeQuery(id+"F4.boolean.opBoolean","SPLIT",FACE,{"disambiguationData":[TD([subQ3])],"derivedFrom":makeQuery(id+"F3.boolean.opBoolean","SPLIT",FACE,{"disambiguationData":[TD([subQ3])],"derivedFrom":makeQuery(id+"F1.opExtrude","CAP_FACE",FACE,{"disambiguationData":[OSD([subQ5,subQ2,subQ0,subQ4,subQ13,sQuery(id+"F0.wireOp",EDGE,"E2"),subQ14,sQuery(id+"F0.wireOp",EDGE,"E4.MirrorC"),subQ6])],"isStart":false})})})],"blendedInto":[makeQuery(id+"F4.boolean.opBoolean","SPLIT",FACE,{"disambiguationData":[TD([subQ3])],"derivedFrom":makeQuery(id+"F3.boolean.opBoolean","SPLIT",FACE,{"disambiguationData":[TD([subQ3])],"derivedFrom":makeQuery(id+"F1.opExtrude","CAP_FACE",FACE,{"disambiguationData":[OSD([subQ5,subQ2,subQ0,subQ4,subQ13,sQuery(id+"F0.wireOp",EDGE,"E2"),subQ14,sQuery(id+"F0.wireOp",EDGE,"E4.MirrorC"),subQ6])],"isStart":false})})})]});}
            fillet(context, id + "F14", {"entities" : qUnion([Q0, Q1, Q2, Q3, Q4, Q5, Q6, Q7, Q8, Q9, Q10, Q11, Q12, Q13, Q14, Q15, Q16, Q17, Q18, Q19, Q20, Q21, Q22, Q23]), "radius" : 1 * mm, "tangentPropagation" : true, "allowEdgeOverflow" : false});
        }
        {
            var Q0;
            Q0=makeQuery(id+"F3.opExtrude","CAP_EDGE",EDGE,{"disambiguationData":[OSD([sQuery(id+"F2.wireOp",EDGE,"E8")])],"isStart":false});
            var Q1;
            Q1=makeQuery(id+"F3.opExtrude","CAP_EDGE",EDGE,{"disambiguationData":[OSD([sQuery(id+"F2.wireOp",EDGE,"E12.MirrorC")])],"isStart":false});
            var Q2;
            Q2=makeQuery(id+"F4.opExtrude","CAP_EDGE",EDGE,{"disambiguationData":[OSD([sQuery(id+"F2.wireOp",EDGE,"E6")])],"isStart":false});
            var Q3;
            Q3=makeQuery(id+"F4.opExtrude","CAP_EDGE",EDGE,{"disambiguationData":[OSD([sQuery(id+"F2.wireOp",EDGE,"E10.MirrorC")])],"isStart":false});
            var Q4;
            Q4=makeQuery(id+"F10.boolean.opBoolean","INTERSECT",EDGE,{"disambiguationData":[OD(1.0)],"derivedFrom":[makeQuery(id+"F4.opExtrude","SWEPT_FACE",FACE,{"disambiguationData":[OSD([sQuery(id+"F2.wireOp",EDGE,"E10.MirrorC")])]}),makeQuery(id+"F10.opExtrude","SWEPT_FACE",FACE,{"disambiguationData":[OSD([sQuery(id+"F9.wireOp",EDGE,"E22.rect.right")])]})]});
            var Q5;
            Q5=makeQuery(id+"F10.boolean.opBoolean","INTERSECT",EDGE,{"disambiguationData":[OD(0.0)],"derivedFrom":[makeQuery(id+"F4.opExtrude","SWEPT_FACE",FACE,{"disambiguationData":[OSD([sQuery(id+"F2.wireOp",EDGE,"E10.MirrorC")])]}),makeQuery(id+"F10.opExtrude","SWEPT_FACE",FACE,{"disambiguationData":[OSD([sQuery(id+"F9.wireOp",EDGE,"E22.rect.right")])]})]});
            var Q6;
            Q6=makeQuery(id+"F10.boolean.opBoolean","INTERSECT",EDGE,{"derivedFrom":[makeQuery(id+"F4.opExtrude","SWEPT_FACE",FACE,{"disambiguationData":[OSD([sQuery(id+"F2.wireOp",EDGE,"E10.MirrorC")])]}),makeQuery(id+"F10.opExtrude","SWEPT_FACE",FACE,{"disambiguationData":[OSD([sQuery(id+"F9.wireOp",EDGE,"E22.rect.top")])]})]});
            var Q7;
            Q7=makeQuery(id+"F10.boolean.opBoolean","INTERSECT",EDGE,{"derivedFrom":[makeQuery(id+"F4.opExtrude","SWEPT_FACE",FACE,{"disambiguationData":[OSD([sQuery(id+"F2.wireOp",EDGE,"E10.MirrorC")])]}),makeQuery(id+"F10.opExtrude","SWEPT_FACE",FACE,{"disambiguationData":[OSD([sQuery(id+"F9.wireOp",EDGE,"E22.rect.bottom")])]})]});
            var Q8;
            Q8=makeQuery(id+"F10.boolean.opBoolean","INTERSECT",EDGE,{"disambiguationData":[OD(0.0)],"derivedFrom":[makeQuery(id+"F4.opExtrude","SWEPT_FACE",FACE,{"disambiguationData":[OSD([sQuery(id+"F2.wireOp",EDGE,"E6")])]}),makeQuery(id+"F10.opExtrude","SWEPT_FACE",FACE,{"disambiguationData":[OSD([sQuery(id+"F9.wireOp",EDGE,"E22.rect.left")])]})]});
            var Q9;
            Q9=makeQuery(id+"F10.boolean.opBoolean","INTERSECT",EDGE,{"disambiguationData":[OD(1.0)],"derivedFrom":[makeQuery(id+"F4.opExtrude","SWEPT_FACE",FACE,{"disambiguationData":[OSD([sQuery(id+"F2.wireOp",EDGE,"E6")])]}),makeQuery(id+"F10.opExtrude","SWEPT_FACE",FACE,{"disambiguationData":[OSD([sQuery(id+"F9.wireOp",EDGE,"E22.rect.left")])]})]});
            var Q10;
            Q10=makeQuery(id+"F10.boolean.opBoolean","INTERSECT",EDGE,{"derivedFrom":[makeQuery(id+"F4.opExtrude","SWEPT_FACE",FACE,{"disambiguationData":[OSD([sQuery(id+"F2.wireOp",EDGE,"E6")])]}),makeQuery(id+"F10.opExtrude","SWEPT_FACE",FACE,{"disambiguationData":[OSD([sQuery(id+"F9.wireOp",EDGE,"E22.rect.top")])]})]});
            var Q11;
            Q11=makeQuery(id+"F10.boolean.opBoolean","INTERSECT",EDGE,{"derivedFrom":[makeQuery(id+"F4.opExtrude","SWEPT_FACE",FACE,{"disambiguationData":[OSD([sQuery(id+"F2.wireOp",EDGE,"E6")])]}),makeQuery(id+"F10.opExtrude","SWEPT_FACE",FACE,{"disambiguationData":[OSD([sQuery(id+"F9.wireOp",EDGE,"E22.rect.bottom")])]})]});
            fillet(context, id + "F15", {"entities" : qUnion([Q0, Q1, Q2, Q3, Q4, Q5, Q6, Q7, Q8, Q9, Q10, Q11]), "radius" : .5 * mm, "tangentPropagation" : true, "allowEdgeOverflow" : false});
        }
        {
            var Q0;
            {var subQ1=sQuery(id+"F5.wireOp",EDGE,"E17");Q0=makeQuery(id+"F12.boolean.opBoolean","INTERSECT",EDGE,{"derivedFrom":[makeQuery(id+"F8.boolean.opBoolean","SPLIT",FACE,{"disambiguationData":[TD([makeQuery(id+"F4.opExtrude","SWEPT_FACE",FACE,{"disambiguationData":[OSD([sQuery(id+"F2.wireOp",EDGE,"E7")])]})])],"derivedFrom":makeQuery(id+"F6.opExtrude","SWEPT_FACE",FACE,{"disambiguationData":[OSD([subQ1])]})}),makeQuery(id+"F12.opExtrude","CAP_FACE",FACE,{"disambiguationData":[OSD([sQuery(id+"F11.wireOp",EDGE,"E23"),sQuery(id+"F11.wireOp",EDGE,"E24"),sQuery(id+"F11.wireOp",EDGE,"E25"),sQuery(id+"F11.wireOp",EDGE,"E26")])],"isStart":false})]});}
            var Q1;
            {var subQ1=sQuery(id+"F5.wireOp",EDGE,"E17");Q1=makeQuery(id+"F12.boolean.opBoolean","INTERSECT",EDGE,{"derivedFrom":[makeQuery(id+"F8.boolean.opBoolean","SPLIT",FACE,{"disambiguationData":[TD([makeQuery(id+"F4.opExtrude","SWEPT_FACE",FACE,{"disambiguationData":[OSD([sQuery(id+"F2.wireOp",EDGE,"E11.MirrorC")])]})])],"derivedFrom":makeQuery(id+"F6.opExtrude","SWEPT_FACE",FACE,{"disambiguationData":[OSD([subQ1])]})}),makeQuery(id+"F12.opExtrude","CAP_FACE",FACE,{"disambiguationData":[OSD([sQuery(id+"F11.wireOp",EDGE,"E27.MirrorCS"),sQuery(id+"F11.wireOp",EDGE,"E28.MirrorCS"),sQuery(id+"F11.wireOp",EDGE,"E29.MirrorCS"),sQuery(id+"F11.wireOp",EDGE,"E30.MirrorCS")])],"isStart":false})]});}
            fillet(context, id + "F16", {"entities" : qUnion([Q0, Q1]), "radius" : 5 * mm, "tangentPropagation" : true, "allowEdgeOverflow" : false});
        }
        {
            var Q0;
            {var subQ0=sQuery(id+"F11.wireOp",EDGE,"E23");var subQ1=sQuery(id+"F2.wireOp",EDGE,"E9");Q0=makeQuery(id+"F12.boolean.opBoolean","SPLIT",EDGE,{"disambiguationData":[TD([makeQuery(id+"F3.opExtrude","SWEPT_FACE",FACE,{"disambiguationData":[OSD([subQ1])]})])],"derivedFrom":makeQuery(id+"F12.opExtrude","CAP_EDGE",EDGE,{"disambiguationData":[OSD([subQ0])],"isStart":false})});}
            var Q1;
            Q1=makeQuery(id+"F12.opExtrude","CAP_EDGE",EDGE,{"disambiguationData":[OSD([sQuery(id+"F11.wireOp",EDGE,"E25")])],"isStart":false});
            var Q2;
            {var subQ0=sQuery(id+"F11.wireOp",EDGE,"E25");var subQ1=sQuery(id+"F5.wireOp",EDGE,"E18");var subQ2=sQuery(id+"F5.wireOp",EDGE,"E17");var subQ3=sQuery(id+"F5.wireOp",EDGE,"E16");var subQ4=makeQuery(id+"F6.opExtrude","CAP_FACE",FACE,{"disambiguationData":[OSD([subQ3,subQ2,subQ1,sQuery(id+"F5.wireOp",EDGE,"E19"),sQuery(id+"F5.wireOp",EDGE,"E20")])],"isStart":true});Q2=makeQuery(id+"F16.opFillet","BLEND_EDGE",EDGE,{"blendedFrom":[makeQuery(id+"F12.boolean.opBoolean","INTERSECT",EDGE,{"derivedFrom":[makeQuery(id+"F8.boolean.opBoolean","SPLIT",FACE,{"disambiguationData":[TD([makeQuery(id+"F4.opExtrude","SWEPT_FACE",FACE,{"disambiguationData":[OSD([sQuery(id+"F2.wireOp",EDGE,"E7")])]})])],"derivedFrom":makeQuery(id+"F6.opExtrude","SWEPT_FACE",FACE,{"disambiguationData":[OSD([subQ2])]})}),makeQuery(id+"F12.opExtrude","CAP_FACE",FACE,{"disambiguationData":[OSD([sQuery(id+"F11.wireOp",EDGE,"E23"),sQuery(id+"F11.wireOp",EDGE,"E24"),subQ0,sQuery(id+"F11.wireOp",EDGE,"E26")])],"isStart":false})]}),makeQuery(id+"F12.boolean.opBoolean","MERGE",FACE,{"derivedFrom":[subQ4,makeQuery(id+"F12.opExtrude","SWEPT_FACE",FACE,{"disambiguationData":[OSD([subQ0])]})]})],"blendedInto":[makeQuery(id+"F12.boolean.opBoolean","MERGE",FACE,{"derivedFrom":[subQ4,makeQuery(id+"F12.opExtrude","SWEPT_FACE",FACE,{"disambiguationData":[OSD([subQ0])]})]})]});}
            var Q3;
            {var subQ0=sQuery(id+"F11.wireOp",EDGE,"E23");var subQ1=makeQuery(id+"F8.opExtrude","SWEPT_FACE",FACE,{"disambiguationData":[OSD([sQuery(id+"F7.wireOp",EDGE,"E21.rect.left")])]});var subQ3=sQuery(id+"F5.wireOp",EDGE,"E17");Q3=makeQuery(id+"F16.opFillet","BLEND_EDGE",EDGE,{"blendedFrom":[makeQuery(id+"F12.boolean.opBoolean","INTERSECT",EDGE,{"derivedFrom":[makeQuery(id+"F8.boolean.opBoolean","SPLIT",FACE,{"disambiguationData":[TD([makeQuery(id+"F4.opExtrude","SWEPT_FACE",FACE,{"disambiguationData":[OSD([sQuery(id+"F2.wireOp",EDGE,"E7")])]})])],"derivedFrom":makeQuery(id+"F6.opExtrude","SWEPT_FACE",FACE,{"disambiguationData":[OSD([subQ3])]})}),makeQuery(id+"F12.opExtrude","CAP_FACE",FACE,{"disambiguationData":[OSD([subQ0,sQuery(id+"F11.wireOp",EDGE,"E24"),sQuery(id+"F11.wireOp",EDGE,"E25"),sQuery(id+"F11.wireOp",EDGE,"E26")])],"isStart":false})]}),makeQuery(id+"F12.boolean.opBoolean","MERGE",FACE,{"derivedFrom":[makeQuery(id+"F8.boolean.opBoolean","COPY",FACE,{"derivedFrom":subQ1}),makeQuery(id+"F12.opExtrude","SWEPT_FACE",FACE,{"disambiguationData":[OSD([subQ0])]})]})],"blendedInto":[makeQuery(id+"F12.boolean.opBoolean","MERGE",FACE,{"derivedFrom":[makeQuery(id+"F8.boolean.opBoolean","COPY",FACE,{"derivedFrom":subQ1}),makeQuery(id+"F12.opExtrude","SWEPT_FACE",FACE,{"disambiguationData":[OSD([subQ0])]})]})]});}
            var Q4;
            Q4=makeQuery(id+"F3.opExtrude","CAP_EDGE",EDGE,{"disambiguationData":[OSD([sQuery(id+"F2.wireOp",EDGE,"E9")])],"isStart":false});
            var Q5;
            Q5=makeQuery(id+"F3.opExtrude","CAP_EDGE",EDGE,{"disambiguationData":[OSD([sQuery(id+"F2.wireOp",EDGE,"E13.MirrorC")])],"isStart":false});
            var Q6;
            {var subQ0=sQuery(id+"F2.wireOp",EDGE,"E13.MirrorC");var subQ1=sQuery(id+"F11.wireOp",EDGE,"E30.MirrorCS");Q6=makeQuery(id+"F12.boolean.opBoolean","SPLIT",EDGE,{"disambiguationData":[TD([makeQuery(id+"F3.opExtrude","SWEPT_FACE",FACE,{"disambiguationData":[OSD([subQ0])]})])],"derivedFrom":makeQuery(id+"F12.opExtrude","CAP_EDGE",EDGE,{"disambiguationData":[OSD([subQ1])],"isStart":false})});}
            var Q7;
            Q7=makeQuery(id+"F12.opExtrude","CAP_EDGE",EDGE,{"disambiguationData":[OSD([sQuery(id+"F11.wireOp",EDGE,"E29.MirrorCS")])],"isStart":false});
            var Q8;
            {var subQ0=sQuery(id+"F11.wireOp",EDGE,"E29.MirrorCS");var subQ1=sQuery(id+"F5.wireOp",EDGE,"E18");var subQ2=sQuery(id+"F5.wireOp",EDGE,"E17");var subQ3=sQuery(id+"F5.wireOp",EDGE,"E16");var subQ4=makeQuery(id+"F6.opExtrude","CAP_FACE",FACE,{"disambiguationData":[OSD([subQ3,subQ2,subQ1,sQuery(id+"F5.wireOp",EDGE,"E19"),sQuery(id+"F5.wireOp",EDGE,"E20")])],"isStart":false});Q8=makeQuery(id+"F16.opFillet","BLEND_EDGE",EDGE,{"blendedFrom":[makeQuery(id+"F12.boolean.opBoolean","INTERSECT",EDGE,{"derivedFrom":[makeQuery(id+"F8.boolean.opBoolean","SPLIT",FACE,{"disambiguationData":[TD([makeQuery(id+"F4.opExtrude","SWEPT_FACE",FACE,{"disambiguationData":[OSD([sQuery(id+"F2.wireOp",EDGE,"E11.MirrorC")])]})])],"derivedFrom":makeQuery(id+"F6.opExtrude","SWEPT_FACE",FACE,{"disambiguationData":[OSD([subQ2])]})}),makeQuery(id+"F12.opExtrude","CAP_FACE",FACE,{"disambiguationData":[OSD([sQuery(id+"F11.wireOp",EDGE,"E27.MirrorCS"),sQuery(id+"F11.wireOp",EDGE,"E28.MirrorCS"),subQ0,sQuery(id+"F11.wireOp",EDGE,"E30.MirrorCS")])],"isStart":false})]}),makeQuery(id+"F12.boolean.opBoolean","MERGE",FACE,{"derivedFrom":[subQ4,makeQuery(id+"F12.opExtrude","SWEPT_FACE",FACE,{"disambiguationData":[OSD([subQ0])]})]})],"blendedInto":[makeQuery(id+"F12.boolean.opBoolean","MERGE",FACE,{"derivedFrom":[subQ4,makeQuery(id+"F12.opExtrude","SWEPT_FACE",FACE,{"disambiguationData":[OSD([subQ0])]})]})]});}
            var Q9;
            {var subQ0=sQuery(id+"F11.wireOp",EDGE,"E30.MirrorCS");var subQ1=makeQuery(id+"F8.opExtrude","SWEPT_FACE",FACE,{"disambiguationData":[OSD([sQuery(id+"F7.wireOp",EDGE,"E21.rect.right")])]});var subQ3=sQuery(id+"F5.wireOp",EDGE,"E17");Q9=makeQuery(id+"F16.opFillet","BLEND_EDGE",EDGE,{"blendedFrom":[makeQuery(id+"F12.boolean.opBoolean","INTERSECT",EDGE,{"derivedFrom":[makeQuery(id+"F8.boolean.opBoolean","SPLIT",FACE,{"disambiguationData":[TD([makeQuery(id+"F4.opExtrude","SWEPT_FACE",FACE,{"disambiguationData":[OSD([sQuery(id+"F2.wireOp",EDGE,"E11.MirrorC")])]})])],"derivedFrom":makeQuery(id+"F6.opExtrude","SWEPT_FACE",FACE,{"disambiguationData":[OSD([subQ3])]})}),makeQuery(id+"F12.opExtrude","CAP_FACE",FACE,{"disambiguationData":[OSD([sQuery(id+"F11.wireOp",EDGE,"E27.MirrorCS"),sQuery(id+"F11.wireOp",EDGE,"E28.MirrorCS"),sQuery(id+"F11.wireOp",EDGE,"E29.MirrorCS"),subQ0])],"isStart":false})]}),makeQuery(id+"F12.boolean.opBoolean","MERGE",FACE,{"derivedFrom":[makeQuery(id+"F8.boolean.opBoolean","COPY",FACE,{"derivedFrom":subQ1}),makeQuery(id+"F12.opExtrude","SWEPT_FACE",FACE,{"disambiguationData":[OSD([subQ0])]})]})],"blendedInto":[makeQuery(id+"F12.boolean.opBoolean","MERGE",FACE,{"derivedFrom":[makeQuery(id+"F8.boolean.opBoolean","COPY",FACE,{"derivedFrom":subQ1}),makeQuery(id+"F12.opExtrude","SWEPT_FACE",FACE,{"disambiguationData":[OSD([subQ0])]})]})]});}
            var Q10;
            Q10=makeQuery(id+"F8.boolean.opBoolean","INTERSECT",EDGE,{"derivedFrom":[makeQuery(id+"F6.opExtrude","SWEPT_FACE",FACE,{"disambiguationData":[OSD([sQuery(id+"F5.wireOp",EDGE,"E17")])]}),makeQuery(id+"F8.opExtrude","SWEPT_FACE",FACE,{"disambiguationData":[OSD([sQuery(id+"F7.wireOp",EDGE,"E21.rect.right")])]})]});
            var Q11;
            Q11=makeQuery(id+"F6.opExtrude","CAP_EDGE",EDGE,{"disambiguationData":[OSD([sQuery(id+"F5.wireOp",EDGE,"E17")])],"isStart":false});
            var Q12;
            Q12=makeQuery(id+"F8.boolean.opBoolean","INTERSECT",EDGE,{"derivedFrom":[makeQuery(id+"F6.opExtrude","SWEPT_FACE",FACE,{"disambiguationData":[OSD([sQuery(id+"F5.wireOp",EDGE,"E16")])]}),makeQuery(id+"F8.opExtrude","SWEPT_FACE",FACE,{"disambiguationData":[OSD([sQuery(id+"F7.wireOp",EDGE,"E21.rect.right")])]})]});
            var Q13;
            Q13=makeQuery(id+"F6.opExtrude","CAP_EDGE",EDGE,{"disambiguationData":[OSD([sQuery(id+"F5.wireOp",EDGE,"E16")])],"isStart":false});
            var Q14;
            Q14=makeQuery(id+"F6.opExtrude","CAP_EDGE",EDGE,{"disambiguationData":[OSD([sQuery(id+"F5.wireOp",EDGE,"E19")])],"isStart":false});
            var Q15;
            Q15=makeQuery(id+"F8.boolean.opBoolean","INTERSECT",EDGE,{"derivedFrom":[makeQuery(id+"F6.opExtrude","SWEPT_FACE",FACE,{"disambiguationData":[OSD([sQuery(id+"F5.wireOp",EDGE,"E19")])]}),makeQuery(id+"F8.opExtrude","SWEPT_FACE",FACE,{"disambiguationData":[OSD([sQuery(id+"F7.wireOp",EDGE,"E21.rect.right")])]})]});
            var Q16;
            Q16=makeQuery(id+"F6.opExtrude","CAP_EDGE",EDGE,{"disambiguationData":[OSD([sQuery(id+"F5.wireOp",EDGE,"E19")])],"isStart":true});
            var Q17;
            Q17=makeQuery(id+"F8.boolean.opBoolean","INTERSECT",EDGE,{"derivedFrom":[makeQuery(id+"F6.opExtrude","SWEPT_FACE",FACE,{"disambiguationData":[OSD([sQuery(id+"F5.wireOp",EDGE,"E19")])]}),makeQuery(id+"F8.opExtrude","SWEPT_FACE",FACE,{"disambiguationData":[OSD([sQuery(id+"F7.wireOp",EDGE,"E21.rect.left")])]})]});
            var Q18;
            Q18=makeQuery(id+"F8.boolean.opBoolean","INTERSECT",EDGE,{"derivedFrom":[makeQuery(id+"F6.opExtrude","SWEPT_FACE",FACE,{"disambiguationData":[OSD([sQuery(id+"F5.wireOp",EDGE,"E16")])]}),makeQuery(id+"F8.opExtrude","SWEPT_FACE",FACE,{"disambiguationData":[OSD([sQuery(id+"F7.wireOp",EDGE,"E21.rect.left")])]})]});
            var Q19;
            Q19=makeQuery(id+"F6.opExtrude","CAP_EDGE",EDGE,{"disambiguationData":[OSD([sQuery(id+"F5.wireOp",EDGE,"E16")])],"isStart":true});
            var Q20;
            Q20=makeQuery(id+"F6.opExtrude","CAP_EDGE",EDGE,{"disambiguationData":[OSD([sQuery(id+"F5.wireOp",EDGE,"E17")])],"isStart":true});
            var Q21;
            Q21=makeQuery(id+"F8.boolean.opBoolean","INTERSECT",EDGE,{"derivedFrom":[makeQuery(id+"F6.opExtrude","SWEPT_FACE",FACE,{"disambiguationData":[OSD([sQuery(id+"F5.wireOp",EDGE,"E17")])]}),makeQuery(id+"F8.opExtrude","SWEPT_FACE",FACE,{"disambiguationData":[OSD([sQuery(id+"F7.wireOp",EDGE,"E21.rect.left")])]})]});
            fillet(context, id + "F17", {"entities" : qUnion([Q0, Q1, Q2, Q3, Q4, Q5, Q6, Q7, Q8, Q9, Q10, Q11, Q12, Q13, Q14, Q15, Q16, Q17, Q18, Q19, Q20, Q21]), "radius" : .75 * mm, "tangentPropagation" : true, "allowEdgeOverflow" : false});
        }
        {
            var Q0;
            {var subQ0=sQuery(id+"F0.wireOp",EDGE,"E0.rect.left");var subQ2=sQuery(id+"F0.wireOp",EDGE,"E0.rect.top");var subQ3=makeQuery(id+"F1.opExtrude","SWEPT_FACE",FACE,{"disambiguationData":[OSD([subQ2])]});var subQ4=sQuery(id+"F0.wireOp",EDGE,"E0.rect.right");var subQ5=sQuery(id+"F0.wireOp",EDGE,"E0.rect.bottom");var subQ6=sQuery(id+"F0.wireOp",EDGE,"E5");var subQ13=sQuery(id+"F0.wireOp",EDGE,"E1");var subQ14=sQuery(id+"F0.wireOp",EDGE,"E3.MirrorC");Q0=makeQuery(id+"F12.boolean.opBoolean","INTERSECT",EDGE,{"derivedFrom":[makeQuery(id+"F4.boolean.opBoolean","SPLIT",FACE,{"disambiguationData":[TD([subQ3])],"derivedFrom":makeQuery(id+"F3.boolean.opBoolean","SPLIT",FACE,{"disambiguationData":[TD([subQ3])],"derivedFrom":makeQuery(id+"F1.opExtrude","CAP_FACE",FACE,{"disambiguationData":[OSD([subQ5,subQ2,subQ0,subQ4,subQ13,sQuery(id+"F0.wireOp",EDGE,"E2"),subQ14,sQuery(id+"F0.wireOp",EDGE,"E4.MirrorC"),subQ6])],"isStart":false})})}),makeQuery(id+"F12.opExtrude","SWEPT_FACE",FACE,{"disambiguationData":[OSD([sQuery(id+"F11.wireOp",EDGE,"E25")])]})]});}
            var Q1;
            {var subQ0=sQuery(id+"F0.wireOp",EDGE,"E0.rect.left");var subQ2=sQuery(id+"F0.wireOp",EDGE,"E0.rect.top");var subQ3=makeQuery(id+"F1.opExtrude","SWEPT_FACE",FACE,{"disambiguationData":[OSD([subQ2])]});var subQ4=sQuery(id+"F0.wireOp",EDGE,"E0.rect.right");var subQ5=sQuery(id+"F0.wireOp",EDGE,"E0.rect.bottom");var subQ6=sQuery(id+"F0.wireOp",EDGE,"E5");var subQ13=sQuery(id+"F0.wireOp",EDGE,"E1");var subQ14=sQuery(id+"F0.wireOp",EDGE,"E3.MirrorC");Q1=makeQuery(id+"F12.boolean.opBoolean","INTERSECT",EDGE,{"derivedFrom":[makeQuery(id+"F4.boolean.opBoolean","SPLIT",FACE,{"disambiguationData":[TD([subQ3])],"derivedFrom":makeQuery(id+"F3.boolean.opBoolean","SPLIT",FACE,{"disambiguationData":[TD([subQ3])],"derivedFrom":makeQuery(id+"F1.opExtrude","CAP_FACE",FACE,{"disambiguationData":[OSD([subQ5,subQ2,subQ0,subQ4,subQ13,sQuery(id+"F0.wireOp",EDGE,"E2"),subQ14,sQuery(id+"F0.wireOp",EDGE,"E4.MirrorC"),subQ6])],"isStart":false})})}),makeQuery(id+"F12.opExtrude","SWEPT_FACE",FACE,{"disambiguationData":[OSD([sQuery(id+"F11.wireOp",EDGE,"E23")])]})]});}
            var Q2;
            {var subQ0=sQuery(id+"F0.wireOp",EDGE,"E0.rect.left");var subQ2=sQuery(id+"F0.wireOp",EDGE,"E0.rect.top");var subQ3=makeQuery(id+"F1.opExtrude","SWEPT_FACE",FACE,{"disambiguationData":[OSD([subQ2])]});var subQ4=sQuery(id+"F0.wireOp",EDGE,"E0.rect.right");var subQ5=sQuery(id+"F0.wireOp",EDGE,"E0.rect.bottom");var subQ6=sQuery(id+"F0.wireOp",EDGE,"E5");var subQ13=sQuery(id+"F0.wireOp",EDGE,"E1");var subQ14=sQuery(id+"F0.wireOp",EDGE,"E3.MirrorC");Q2=makeQuery(id+"F12.boolean.opBoolean","INTERSECT",EDGE,{"derivedFrom":[makeQuery(id+"F4.boolean.opBoolean","SPLIT",FACE,{"disambiguationData":[TD([subQ3])],"derivedFrom":makeQuery(id+"F3.boolean.opBoolean","SPLIT",FACE,{"disambiguationData":[TD([subQ3])],"derivedFrom":makeQuery(id+"F1.opExtrude","CAP_FACE",FACE,{"disambiguationData":[OSD([subQ5,subQ2,subQ0,subQ4,subQ13,sQuery(id+"F0.wireOp",EDGE,"E2"),subQ14,sQuery(id+"F0.wireOp",EDGE,"E4.MirrorC"),subQ6])],"isStart":false})})}),makeQuery(id+"F12.opExtrude","SWEPT_FACE",FACE,{"disambiguationData":[OSD([sQuery(id+"F11.wireOp",EDGE,"E29.MirrorCS")])]})]});}
            var Q3;
            {var subQ0=sQuery(id+"F0.wireOp",EDGE,"E0.rect.left");var subQ2=sQuery(id+"F0.wireOp",EDGE,"E0.rect.top");var subQ3=makeQuery(id+"F1.opExtrude","SWEPT_FACE",FACE,{"disambiguationData":[OSD([subQ2])]});var subQ4=sQuery(id+"F0.wireOp",EDGE,"E0.rect.right");var subQ5=sQuery(id+"F0.wireOp",EDGE,"E0.rect.bottom");var subQ6=sQuery(id+"F0.wireOp",EDGE,"E5");var subQ13=sQuery(id+"F0.wireOp",EDGE,"E1");var subQ14=sQuery(id+"F0.wireOp",EDGE,"E3.MirrorC");Q3=makeQuery(id+"F12.boolean.opBoolean","INTERSECT",EDGE,{"derivedFrom":[makeQuery(id+"F4.boolean.opBoolean","SPLIT",FACE,{"disambiguationData":[TD([subQ3])],"derivedFrom":makeQuery(id+"F3.boolean.opBoolean","SPLIT",FACE,{"disambiguationData":[TD([subQ3])],"derivedFrom":makeQuery(id+"F1.opExtrude","CAP_FACE",FACE,{"disambiguationData":[OSD([subQ5,subQ2,subQ0,subQ4,subQ13,sQuery(id+"F0.wireOp",EDGE,"E2"),subQ14,sQuery(id+"F0.wireOp",EDGE,"E4.MirrorC"),subQ6])],"isStart":false})})}),makeQuery(id+"F12.opExtrude","SWEPT_FACE",FACE,{"disambiguationData":[OSD([sQuery(id+"F11.wireOp",EDGE,"E30.MirrorCS")])]})]});}
            var Q4;
            Q4=makeQuery(id+"F4.opExtrude","CAP_EDGE",EDGE,{"disambiguationData":[OSD([sQuery(id+"F2.wireOp",EDGE,"E11.MirrorC")])],"isStart":true});
            var Q5;
            Q5=makeQuery(id+"F4.opExtrude","CAP_EDGE",EDGE,{"disambiguationData":[OSD([sQuery(id+"F2.wireOp",EDGE,"E7")])],"isStart":true});
            var Q6;
            Q6=makeQuery(id+"F3.opExtrude","CAP_EDGE",EDGE,{"disambiguationData":[OSD([sQuery(id+"F2.wireOp",EDGE,"E13.MirrorC")])],"isStart":true});
            var Q7;
            Q7=makeQuery(id+"F3.opExtrude","CAP_EDGE",EDGE,{"disambiguationData":[OSD([sQuery(id+"F2.wireOp",EDGE,"E9")])],"isStart":true});
            var Q8;
            Q8=makeQuery(id+"F14.opFillet","BLEND_EDGE",EDGE,{"blendedFrom":[makeQuery(id+"F1.opExtrude","CAP_EDGE",EDGE,{"disambiguationData":[OSD([sQuery(id+"F0.wireOp",EDGE,"E0.rect.left")])],"isStart":false}),makeQuery(id+"F4.opExtrude","SWEPT_FACE",FACE,{"disambiguationData":[OSD([sQuery(id+"F2.wireOp",EDGE,"E11.MirrorC")])]})],"blendedInto":[makeQuery(id+"F4.opExtrude","SWEPT_FACE",FACE,{"disambiguationData":[OSD([sQuery(id+"F2.wireOp",EDGE,"E11.MirrorC")])]})]});
            var Q9;
            {var subQ0=makeQuery(id+"F4.opExtrude","SWEPT_FACE",FACE,{"disambiguationData":[OSD([sQuery(id+"F2.wireOp",EDGE,"E11.MirrorC")])]});var subQ1=sQuery(id+"F0.wireOp",EDGE,"E0.rect.left");var subQ3=sQuery(id+"F0.wireOp",EDGE,"E0.rect.top");var subQ4=makeQuery(id+"F1.opExtrude","SWEPT_FACE",FACE,{"disambiguationData":[OSD([subQ3])]});var subQ5=sQuery(id+"F0.wireOp",EDGE,"E0.rect.right");var subQ6=sQuery(id+"F0.wireOp",EDGE,"E0.rect.bottom");var subQ7=sQuery(id+"F0.wireOp",EDGE,"E5");var subQ14=sQuery(id+"F0.wireOp",EDGE,"E1");var subQ15=sQuery(id+"F0.wireOp",EDGE,"E3.MirrorC");Q9=makeQuery(id+"F14.opFillet","BLEND_EDGE",EDGE,{"disambiguationData":[OD(1.0)],"blendedFrom":[makeQuery(id+"F13.opFillet","BLEND_EDGE",EDGE,{"blendedFrom":[makeQuery(id+"F1.opExtrude","SWEPT_EDGE",EDGE,{"disambiguationData":[OSD([subQ6,subQ1])]}),makeQuery(id+"F4.boolean.opBoolean","SPLIT",FACE,{"disambiguationData":[TD([subQ4])],"derivedFrom":makeQuery(id+"F3.boolean.opBoolean","SPLIT",FACE,{"disambiguationData":[TD([subQ4])],"derivedFrom":makeQuery(id+"F1.opExtrude","CAP_FACE",FACE,{"disambiguationData":[OSD([subQ6,subQ3,subQ1,subQ5,subQ14,sQuery(id+"F0.wireOp",EDGE,"E2"),subQ15,sQuery(id+"F0.wireOp",EDGE,"E4.MirrorC"),subQ7])],"isStart":false})})})],"blendedInto":[makeQuery(id+"F4.boolean.opBoolean","SPLIT",FACE,{"disambiguationData":[TD([subQ4])],"derivedFrom":makeQuery(id+"F3.boolean.opBoolean","SPLIT",FACE,{"disambiguationData":[TD([subQ4])],"derivedFrom":makeQuery(id+"F1.opExtrude","CAP_FACE",FACE,{"disambiguationData":[OSD([subQ6,subQ3,subQ1,subQ5,subQ14,sQuery(id+"F0.wireOp",EDGE,"E2"),subQ15,sQuery(id+"F0.wireOp",EDGE,"E4.MirrorC"),subQ7])],"isStart":false})})})]}),subQ0],"blendedInto":[subQ0]});}
            var Q10;
            {var subQ0=makeQuery(id+"F4.opExtrude","SWEPT_FACE",FACE,{"disambiguationData":[OSD([sQuery(id+"F2.wireOp",EDGE,"E11.MirrorC")])]});var subQ1=sQuery(id+"F0.wireOp",EDGE,"E0.rect.left");var subQ3=sQuery(id+"F0.wireOp",EDGE,"E0.rect.top");var subQ4=makeQuery(id+"F1.opExtrude","SWEPT_FACE",FACE,{"disambiguationData":[OSD([subQ3])]});var subQ5=sQuery(id+"F0.wireOp",EDGE,"E0.rect.right");var subQ6=sQuery(id+"F0.wireOp",EDGE,"E0.rect.bottom");var subQ7=sQuery(id+"F0.wireOp",EDGE,"E5");var subQ14=sQuery(id+"F0.wireOp",EDGE,"E1");var subQ15=sQuery(id+"F0.wireOp",EDGE,"E3.MirrorC");Q10=makeQuery(id+"F14.opFillet","BLEND_EDGE",EDGE,{"disambiguationData":[OD(0.0)],"blendedFrom":[makeQuery(id+"F13.opFillet","BLEND_EDGE",EDGE,{"blendedFrom":[makeQuery(id+"F1.opExtrude","SWEPT_EDGE",EDGE,{"disambiguationData":[OSD([subQ6,subQ1])]}),makeQuery(id+"F4.boolean.opBoolean","SPLIT",FACE,{"disambiguationData":[TD([subQ4])],"derivedFrom":makeQuery(id+"F3.boolean.opBoolean","SPLIT",FACE,{"disambiguationData":[TD([subQ4])],"derivedFrom":makeQuery(id+"F1.opExtrude","CAP_FACE",FACE,{"disambiguationData":[OSD([subQ6,subQ3,subQ1,subQ5,subQ14,sQuery(id+"F0.wireOp",EDGE,"E2"),subQ15,sQuery(id+"F0.wireOp",EDGE,"E4.MirrorC"),subQ7])],"isStart":false})})})],"blendedInto":[makeQuery(id+"F4.boolean.opBoolean","SPLIT",FACE,{"disambiguationData":[TD([subQ4])],"derivedFrom":makeQuery(id+"F3.boolean.opBoolean","SPLIT",FACE,{"disambiguationData":[TD([subQ4])],"derivedFrom":makeQuery(id+"F1.opExtrude","CAP_FACE",FACE,{"disambiguationData":[OSD([subQ6,subQ3,subQ1,subQ5,subQ14,sQuery(id+"F0.wireOp",EDGE,"E2"),subQ15,sQuery(id+"F0.wireOp",EDGE,"E4.MirrorC"),subQ7])],"isStart":false})})})]}),subQ0],"blendedInto":[subQ0]});}
            var Q11;
            {var subQ0=sQuery(id+"F0.wireOp",EDGE,"E0.rect.bottom");Q11=makeQuery(id+"F14.opFillet","BLEND_EDGE",EDGE,{"blendedFrom":[makeQuery(id+"F1.opExtrude","CAP_EDGE",EDGE,{"disambiguationData":[OSD([subQ0]),TDD([makeQuery(id+"F0.imprint","IMPRINT",EDGE,{"disambiguationData":[TD([[makeQuery(id+"F0.imprint","INTERSECT",VERTEX,{"derivedFrom":[subQ0,sQuery(id+"F0.wireOp",EDGE,"E0.rect.left")]}),-1.0]])],"derivedFrom":subQ0})])],"isStart":false}),makeQuery(id+"F4.opExtrude","SWEPT_FACE",FACE,{"disambiguationData":[OSD([sQuery(id+"F2.wireOp",EDGE,"E11.MirrorC")])]})],"blendedInto":[makeQuery(id+"F4.opExtrude","SWEPT_FACE",FACE,{"disambiguationData":[OSD([sQuery(id+"F2.wireOp",EDGE,"E11.MirrorC")])]})]});}
            var Q12;
            Q12=makeQuery(id+"F14.opFillet","BLEND_EDGE",EDGE,{"blendedFrom":[makeQuery(id+"F1.opExtrude","CAP_EDGE",EDGE,{"disambiguationData":[OSD([sQuery(id+"F0.wireOp",EDGE,"E0.rect.left")])],"isStart":false}),makeQuery(id+"F3.opExtrude","SWEPT_FACE",FACE,{"disambiguationData":[OSD([sQuery(id+"F2.wireOp",EDGE,"E13.MirrorC")])]})],"blendedInto":[makeQuery(id+"F3.opExtrude","SWEPT_FACE",FACE,{"disambiguationData":[OSD([sQuery(id+"F2.wireOp",EDGE,"E13.MirrorC")])]})]});
            var Q13;
            {var subQ0=makeQuery(id+"F3.opExtrude","SWEPT_FACE",FACE,{"disambiguationData":[OSD([sQuery(id+"F2.wireOp",EDGE,"E13.MirrorC")])]});var subQ1=sQuery(id+"F0.wireOp",EDGE,"E0.rect.left");var subQ3=sQuery(id+"F0.wireOp",EDGE,"E0.rect.top");var subQ4=makeQuery(id+"F1.opExtrude","SWEPT_FACE",FACE,{"disambiguationData":[OSD([subQ3])]});var subQ5=sQuery(id+"F0.wireOp",EDGE,"E0.rect.right");var subQ6=sQuery(id+"F0.wireOp",EDGE,"E0.rect.bottom");var subQ7=sQuery(id+"F0.wireOp",EDGE,"E5");var subQ13=sQuery(id+"F0.wireOp",EDGE,"E1");var subQ14=sQuery(id+"F0.wireOp",EDGE,"E3.MirrorC");Q13=makeQuery(id+"F14.opFillet","BLEND_EDGE",EDGE,{"disambiguationData":[OD(1.0)],"blendedFrom":[makeQuery(id+"F13.opFillet","BLEND_EDGE",EDGE,{"blendedFrom":[makeQuery(id+"F1.opExtrude","SWEPT_EDGE",EDGE,{"disambiguationData":[OSD([subQ3,subQ1])]}),makeQuery(id+"F4.boolean.opBoolean","SPLIT",FACE,{"disambiguationData":[TD([subQ4])],"derivedFrom":makeQuery(id+"F3.boolean.opBoolean","SPLIT",FACE,{"disambiguationData":[TD([subQ4])],"derivedFrom":makeQuery(id+"F1.opExtrude","CAP_FACE",FACE,{"disambiguationData":[OSD([subQ6,subQ3,subQ1,subQ5,subQ13,sQuery(id+"F0.wireOp",EDGE,"E2"),subQ14,sQuery(id+"F0.wireOp",EDGE,"E4.MirrorC"),subQ7])],"isStart":false})})})],"blendedInto":[makeQuery(id+"F4.boolean.opBoolean","SPLIT",FACE,{"disambiguationData":[TD([subQ4])],"derivedFrom":makeQuery(id+"F3.boolean.opBoolean","SPLIT",FACE,{"disambiguationData":[TD([subQ4])],"derivedFrom":makeQuery(id+"F1.opExtrude","CAP_FACE",FACE,{"disambiguationData":[OSD([subQ6,subQ3,subQ1,subQ5,subQ13,sQuery(id+"F0.wireOp",EDGE,"E2"),subQ14,sQuery(id+"F0.wireOp",EDGE,"E4.MirrorC"),subQ7])],"isStart":false})})})]}),subQ0],"blendedInto":[subQ0]});}
            var Q14;
            {var subQ0=makeQuery(id+"F3.opExtrude","SWEPT_FACE",FACE,{"disambiguationData":[OSD([sQuery(id+"F2.wireOp",EDGE,"E13.MirrorC")])]});var subQ1=sQuery(id+"F0.wireOp",EDGE,"E0.rect.left");var subQ3=sQuery(id+"F0.wireOp",EDGE,"E0.rect.top");var subQ4=makeQuery(id+"F1.opExtrude","SWEPT_FACE",FACE,{"disambiguationData":[OSD([subQ3])]});var subQ5=sQuery(id+"F0.wireOp",EDGE,"E0.rect.right");var subQ6=sQuery(id+"F0.wireOp",EDGE,"E0.rect.bottom");var subQ7=sQuery(id+"F0.wireOp",EDGE,"E5");var subQ13=sQuery(id+"F0.wireOp",EDGE,"E1");var subQ14=sQuery(id+"F0.wireOp",EDGE,"E3.MirrorC");Q14=makeQuery(id+"F14.opFillet","BLEND_EDGE",EDGE,{"disambiguationData":[OD(0.0)],"blendedFrom":[makeQuery(id+"F13.opFillet","BLEND_EDGE",EDGE,{"blendedFrom":[makeQuery(id+"F1.opExtrude","SWEPT_EDGE",EDGE,{"disambiguationData":[OSD([subQ3,subQ1])]}),makeQuery(id+"F4.boolean.opBoolean","SPLIT",FACE,{"disambiguationData":[TD([subQ4])],"derivedFrom":makeQuery(id+"F3.boolean.opBoolean","SPLIT",FACE,{"disambiguationData":[TD([subQ4])],"derivedFrom":makeQuery(id+"F1.opExtrude","CAP_FACE",FACE,{"disambiguationData":[OSD([subQ6,subQ3,subQ1,subQ5,subQ13,sQuery(id+"F0.wireOp",EDGE,"E2"),subQ14,sQuery(id+"F0.wireOp",EDGE,"E4.MirrorC"),subQ7])],"isStart":false})})})],"blendedInto":[makeQuery(id+"F4.boolean.opBoolean","SPLIT",FACE,{"disambiguationData":[TD([subQ4])],"derivedFrom":makeQuery(id+"F3.boolean.opBoolean","SPLIT",FACE,{"disambiguationData":[TD([subQ4])],"derivedFrom":makeQuery(id+"F1.opExtrude","CAP_FACE",FACE,{"disambiguationData":[OSD([subQ6,subQ3,subQ1,subQ5,subQ13,sQuery(id+"F0.wireOp",EDGE,"E2"),subQ14,sQuery(id+"F0.wireOp",EDGE,"E4.MirrorC"),subQ7])],"isStart":false})})})]}),subQ0],"blendedInto":[subQ0]});}
            var Q15;
            Q15=makeQuery(id+"F3.opExtrude","SWEPT_FACE",FACE,{"disambiguationData":[OSD([sQuery(id+"F2.wireOp",EDGE,"E13.MirrorC")])]});
            var Q16;
            Q16=makeQuery(id+"F14.opFillet","BLEND_EDGE",EDGE,{"blendedFrom":[makeQuery(id+"F1.opExtrude","CAP_EDGE",EDGE,{"disambiguationData":[OSD([sQuery(id+"F0.wireOp",EDGE,"E0.rect.top")])],"isStart":false}),makeQuery(id+"F3.opExtrude","SWEPT_FACE",FACE,{"disambiguationData":[OSD([sQuery(id+"F2.wireOp",EDGE,"E13.MirrorC")])]})],"blendedInto":[makeQuery(id+"F3.opExtrude","SWEPT_FACE",FACE,{"disambiguationData":[OSD([sQuery(id+"F2.wireOp",EDGE,"E13.MirrorC")])]})]});
            var Q17;
            Q17=makeQuery(id+"F14.opFillet","BLEND_EDGE",EDGE,{"blendedFrom":[makeQuery(id+"F1.opExtrude","CAP_EDGE",EDGE,{"disambiguationData":[OSD([sQuery(id+"F0.wireOp",EDGE,"E0.rect.top")])],"isStart":false}),makeQuery(id+"F3.opExtrude","SWEPT_FACE",FACE,{"disambiguationData":[OSD([sQuery(id+"F2.wireOp",EDGE,"E9")])]})],"blendedInto":[makeQuery(id+"F3.opExtrude","SWEPT_FACE",FACE,{"disambiguationData":[OSD([sQuery(id+"F2.wireOp",EDGE,"E9")])]})]});
            var Q18;
            {var subQ0=makeQuery(id+"F3.opExtrude","SWEPT_FACE",FACE,{"disambiguationData":[OSD([sQuery(id+"F2.wireOp",EDGE,"E9")])]});var subQ1=sQuery(id+"F0.wireOp",EDGE,"E0.rect.left");var subQ3=sQuery(id+"F0.wireOp",EDGE,"E0.rect.top");var subQ4=makeQuery(id+"F1.opExtrude","SWEPT_FACE",FACE,{"disambiguationData":[OSD([subQ3])]});var subQ5=sQuery(id+"F0.wireOp",EDGE,"E0.rect.right");var subQ6=sQuery(id+"F0.wireOp",EDGE,"E0.rect.bottom");var subQ7=sQuery(id+"F0.wireOp",EDGE,"E5");var subQ13=sQuery(id+"F0.wireOp",EDGE,"E1");var subQ14=sQuery(id+"F0.wireOp",EDGE,"E3.MirrorC");Q18=makeQuery(id+"F14.opFillet","BLEND_EDGE",EDGE,{"disambiguationData":[OD(0.0)],"blendedFrom":[makeQuery(id+"F13.opFillet","BLEND_EDGE",EDGE,{"blendedFrom":[makeQuery(id+"F1.opExtrude","SWEPT_EDGE",EDGE,{"disambiguationData":[OSD([subQ3,subQ5])]}),makeQuery(id+"F4.boolean.opBoolean","SPLIT",FACE,{"disambiguationData":[TD([subQ4])],"derivedFrom":makeQuery(id+"F3.boolean.opBoolean","SPLIT",FACE,{"disambiguationData":[TD([subQ4])],"derivedFrom":makeQuery(id+"F1.opExtrude","CAP_FACE",FACE,{"disambiguationData":[OSD([subQ6,subQ3,subQ1,subQ5,subQ13,sQuery(id+"F0.wireOp",EDGE,"E2"),subQ14,sQuery(id+"F0.wireOp",EDGE,"E4.MirrorC"),subQ7])],"isStart":false})})})],"blendedInto":[makeQuery(id+"F4.boolean.opBoolean","SPLIT",FACE,{"disambiguationData":[TD([subQ4])],"derivedFrom":makeQuery(id+"F3.boolean.opBoolean","SPLIT",FACE,{"disambiguationData":[TD([subQ4])],"derivedFrom":makeQuery(id+"F1.opExtrude","CAP_FACE",FACE,{"disambiguationData":[OSD([subQ6,subQ3,subQ1,subQ5,subQ13,sQuery(id+"F0.wireOp",EDGE,"E2"),subQ14,sQuery(id+"F0.wireOp",EDGE,"E4.MirrorC"),subQ7])],"isStart":false})})})]}),subQ0],"blendedInto":[subQ0]});}
            var Q19;
            {var subQ0=makeQuery(id+"F3.opExtrude","SWEPT_FACE",FACE,{"disambiguationData":[OSD([sQuery(id+"F2.wireOp",EDGE,"E9")])]});var subQ1=sQuery(id+"F0.wireOp",EDGE,"E0.rect.left");var subQ3=sQuery(id+"F0.wireOp",EDGE,"E0.rect.top");var subQ4=makeQuery(id+"F1.opExtrude","SWEPT_FACE",FACE,{"disambiguationData":[OSD([subQ3])]});var subQ5=sQuery(id+"F0.wireOp",EDGE,"E0.rect.right");var subQ6=sQuery(id+"F0.wireOp",EDGE,"E0.rect.bottom");var subQ7=sQuery(id+"F0.wireOp",EDGE,"E5");var subQ13=sQuery(id+"F0.wireOp",EDGE,"E1");var subQ14=sQuery(id+"F0.wireOp",EDGE,"E3.MirrorC");Q19=makeQuery(id+"F14.opFillet","BLEND_EDGE",EDGE,{"disambiguationData":[OD(1.0)],"blendedFrom":[makeQuery(id+"F13.opFillet","BLEND_EDGE",EDGE,{"blendedFrom":[makeQuery(id+"F1.opExtrude","SWEPT_EDGE",EDGE,{"disambiguationData":[OSD([subQ3,subQ5])]}),makeQuery(id+"F4.boolean.opBoolean","SPLIT",FACE,{"disambiguationData":[TD([subQ4])],"derivedFrom":makeQuery(id+"F3.boolean.opBoolean","SPLIT",FACE,{"disambiguationData":[TD([subQ4])],"derivedFrom":makeQuery(id+"F1.opExtrude","CAP_FACE",FACE,{"disambiguationData":[OSD([subQ6,subQ3,subQ1,subQ5,subQ13,sQuery(id+"F0.wireOp",EDGE,"E2"),subQ14,sQuery(id+"F0.wireOp",EDGE,"E4.MirrorC"),subQ7])],"isStart":false})})})],"blendedInto":[makeQuery(id+"F4.boolean.opBoolean","SPLIT",FACE,{"disambiguationData":[TD([subQ4])],"derivedFrom":makeQuery(id+"F3.boolean.opBoolean","SPLIT",FACE,{"disambiguationData":[TD([subQ4])],"derivedFrom":makeQuery(id+"F1.opExtrude","CAP_FACE",FACE,{"disambiguationData":[OSD([subQ6,subQ3,subQ1,subQ5,subQ13,sQuery(id+"F0.wireOp",EDGE,"E2"),subQ14,sQuery(id+"F0.wireOp",EDGE,"E4.MirrorC"),subQ7])],"isStart":false})})})]}),subQ0],"blendedInto":[subQ0]});}
            var Q20;
            Q20=makeQuery(id+"F14.opFillet","BLEND_EDGE",EDGE,{"blendedFrom":[makeQuery(id+"F1.opExtrude","CAP_EDGE",EDGE,{"disambiguationData":[OSD([sQuery(id+"F0.wireOp",EDGE,"E0.rect.right")])],"isStart":false}),makeQuery(id+"F3.opExtrude","SWEPT_FACE",FACE,{"disambiguationData":[OSD([sQuery(id+"F2.wireOp",EDGE,"E9")])]})],"blendedInto":[makeQuery(id+"F3.opExtrude","SWEPT_FACE",FACE,{"disambiguationData":[OSD([sQuery(id+"F2.wireOp",EDGE,"E9")])]})]});
            var Q21;
            Q21=makeQuery(id+"F14.opFillet","BLEND_EDGE",EDGE,{"blendedFrom":[makeQuery(id+"F1.opExtrude","CAP_EDGE",EDGE,{"disambiguationData":[OSD([sQuery(id+"F0.wireOp",EDGE,"E0.rect.right")])],"isStart":false}),makeQuery(id+"F4.opExtrude","SWEPT_FACE",FACE,{"disambiguationData":[OSD([sQuery(id+"F2.wireOp",EDGE,"E7")])]})],"blendedInto":[makeQuery(id+"F4.opExtrude","SWEPT_FACE",FACE,{"disambiguationData":[OSD([sQuery(id+"F2.wireOp",EDGE,"E7")])]})]});
            var Q22;
            {var subQ0=makeQuery(id+"F4.opExtrude","SWEPT_FACE",FACE,{"disambiguationData":[OSD([sQuery(id+"F2.wireOp",EDGE,"E7")])]});var subQ1=sQuery(id+"F0.wireOp",EDGE,"E0.rect.left");var subQ3=sQuery(id+"F0.wireOp",EDGE,"E0.rect.top");var subQ4=makeQuery(id+"F1.opExtrude","SWEPT_FACE",FACE,{"disambiguationData":[OSD([subQ3])]});var subQ5=sQuery(id+"F0.wireOp",EDGE,"E0.rect.right");var subQ6=sQuery(id+"F0.wireOp",EDGE,"E0.rect.bottom");var subQ7=sQuery(id+"F0.wireOp",EDGE,"E5");var subQ14=sQuery(id+"F0.wireOp",EDGE,"E1");var subQ15=sQuery(id+"F0.wireOp",EDGE,"E3.MirrorC");Q22=makeQuery(id+"F14.opFillet","BLEND_EDGE",EDGE,{"disambiguationData":[OD(1.0)],"blendedFrom":[makeQuery(id+"F13.opFillet","BLEND_EDGE",EDGE,{"blendedFrom":[makeQuery(id+"F1.opExtrude","SWEPT_EDGE",EDGE,{"disambiguationData":[OSD([subQ6,subQ5])]}),makeQuery(id+"F4.boolean.opBoolean","SPLIT",FACE,{"disambiguationData":[TD([subQ4])],"derivedFrom":makeQuery(id+"F3.boolean.opBoolean","SPLIT",FACE,{"disambiguationData":[TD([subQ4])],"derivedFrom":makeQuery(id+"F1.opExtrude","CAP_FACE",FACE,{"disambiguationData":[OSD([subQ6,subQ3,subQ1,subQ5,subQ14,sQuery(id+"F0.wireOp",EDGE,"E2"),subQ15,sQuery(id+"F0.wireOp",EDGE,"E4.MirrorC"),subQ7])],"isStart":false})})})],"blendedInto":[makeQuery(id+"F4.boolean.opBoolean","SPLIT",FACE,{"disambiguationData":[TD([subQ4])],"derivedFrom":makeQuery(id+"F3.boolean.opBoolean","SPLIT",FACE,{"disambiguationData":[TD([subQ4])],"derivedFrom":makeQuery(id+"F1.opExtrude","CAP_FACE",FACE,{"disambiguationData":[OSD([subQ6,subQ3,subQ1,subQ5,subQ14,sQuery(id+"F0.wireOp",EDGE,"E2"),subQ15,sQuery(id+"F0.wireOp",EDGE,"E4.MirrorC"),subQ7])],"isStart":false})})})]}),subQ0],"blendedInto":[subQ0]});}
            var Q23;
            {var subQ0=makeQuery(id+"F4.opExtrude","SWEPT_FACE",FACE,{"disambiguationData":[OSD([sQuery(id+"F2.wireOp",EDGE,"E7")])]});var subQ1=sQuery(id+"F0.wireOp",EDGE,"E0.rect.left");var subQ3=sQuery(id+"F0.wireOp",EDGE,"E0.rect.top");var subQ4=makeQuery(id+"F1.opExtrude","SWEPT_FACE",FACE,{"disambiguationData":[OSD([subQ3])]});var subQ5=sQuery(id+"F0.wireOp",EDGE,"E0.rect.right");var subQ6=sQuery(id+"F0.wireOp",EDGE,"E0.rect.bottom");var subQ7=sQuery(id+"F0.wireOp",EDGE,"E5");var subQ14=sQuery(id+"F0.wireOp",EDGE,"E1");var subQ15=sQuery(id+"F0.wireOp",EDGE,"E3.MirrorC");Q23=makeQuery(id+"F14.opFillet","BLEND_EDGE",EDGE,{"disambiguationData":[OD(0.0)],"blendedFrom":[makeQuery(id+"F13.opFillet","BLEND_EDGE",EDGE,{"blendedFrom":[makeQuery(id+"F1.opExtrude","SWEPT_EDGE",EDGE,{"disambiguationData":[OSD([subQ6,subQ5])]}),makeQuery(id+"F4.boolean.opBoolean","SPLIT",FACE,{"disambiguationData":[TD([subQ4])],"derivedFrom":makeQuery(id+"F3.boolean.opBoolean","SPLIT",FACE,{"disambiguationData":[TD([subQ4])],"derivedFrom":makeQuery(id+"F1.opExtrude","CAP_FACE",FACE,{"disambiguationData":[OSD([subQ6,subQ3,subQ1,subQ5,subQ14,sQuery(id+"F0.wireOp",EDGE,"E2"),subQ15,sQuery(id+"F0.wireOp",EDGE,"E4.MirrorC"),subQ7])],"isStart":false})})})],"blendedInto":[makeQuery(id+"F4.boolean.opBoolean","SPLIT",FACE,{"disambiguationData":[TD([subQ4])],"derivedFrom":makeQuery(id+"F3.boolean.opBoolean","SPLIT",FACE,{"disambiguationData":[TD([subQ4])],"derivedFrom":makeQuery(id+"F1.opExtrude","CAP_FACE",FACE,{"disambiguationData":[OSD([subQ6,subQ3,subQ1,subQ5,subQ14,sQuery(id+"F0.wireOp",EDGE,"E2"),subQ15,sQuery(id+"F0.wireOp",EDGE,"E4.MirrorC"),subQ7])],"isStart":false})})})]}),subQ0],"blendedInto":[subQ0]});}
            var Q24;
            {var subQ0=sQuery(id+"F0.wireOp",EDGE,"E0.rect.bottom");Q24=makeQuery(id+"F14.opFillet","BLEND_EDGE",EDGE,{"blendedFrom":[makeQuery(id+"F1.opExtrude","CAP_EDGE",EDGE,{"disambiguationData":[OSD([subQ0]),TDD([makeQuery(id+"F0.imprint","IMPRINT",EDGE,{"disambiguationData":[TD([[makeQuery(id+"F0.imprint","INTERSECT",VERTEX,{"derivedFrom":[subQ0,sQuery(id+"F0.wireOp",EDGE,"E0.rect.right")]}),1.0]])],"derivedFrom":subQ0})])],"isStart":false}),makeQuery(id+"F4.opExtrude","SWEPT_FACE",FACE,{"disambiguationData":[OSD([sQuery(id+"F2.wireOp",EDGE,"E7")])]})],"blendedInto":[makeQuery(id+"F4.opExtrude","SWEPT_FACE",FACE,{"disambiguationData":[OSD([sQuery(id+"F2.wireOp",EDGE,"E7")])]})]});}
            fillet(context, id + "F18", {"entities" : qUnion([Q0, Q1, Q2, Q3, Q4, Q5, Q6, Q7, Q8, Q9, Q10, Q11, Q12, Q13, Q14, Q15, Q16, Q17, Q18, Q19, Q20, Q21, Q22, Q23, Q24]), "radius" : 3 * mm, "tangentPropagation" : true, "allowEdgeOverflow" : false});
        }
        {
            var Q0;
            Q0=makeQuery(id+"F10.boolean.opBoolean","COPY",EDGE,{"disambiguationData":[OD(0.0)],"derivedFrom":makeQuery(id+"F10.opExtrude","SWEPT_EDGE",EDGE,{"disambiguationData":[OSD([sQuery(id+"F9.wireOp",EDGE,"E22.rect.top"),sQuery(id+"F9.wireOp",EDGE,"E22.rect.right")])]})});
            var Q1;
            Q1=makeQuery(id+"F10.boolean.opBoolean","COPY",EDGE,{"disambiguationData":[OD(1.0)],"derivedFrom":makeQuery(id+"F10.opExtrude","SWEPT_EDGE",EDGE,{"disambiguationData":[OSD([sQuery(id+"F9.wireOp",EDGE,"E22.rect.top"),sQuery(id+"F9.wireOp",EDGE,"E22.rect.right")])]})});
            var Q2;
            Q2=makeQuery(id+"F10.boolean.opBoolean","COPY",EDGE,{"disambiguationData":[OD(1.0)],"derivedFrom":makeQuery(id+"F10.opExtrude","SWEPT_EDGE",EDGE,{"disambiguationData":[OSD([sQuery(id+"F9.wireOp",EDGE,"E22.rect.top"),sQuery(id+"F9.wireOp",EDGE,"E22.rect.left")])]})});
            var Q3;
            Q3=makeQuery(id+"F10.boolean.opBoolean","COPY",EDGE,{"disambiguationData":[OD(0.0)],"derivedFrom":makeQuery(id+"F10.opExtrude","SWEPT_EDGE",EDGE,{"disambiguationData":[OSD([sQuery(id+"F9.wireOp",EDGE,"E22.rect.top"),sQuery(id+"F9.wireOp",EDGE,"E22.rect.left")])]})});
            var Q4;
            Q4=makeQuery(id+"F10.boolean.opBoolean","COPY",EDGE,{"disambiguationData":[OD(0.0)],"derivedFrom":makeQuery(id+"F10.opExtrude","SWEPT_EDGE",EDGE,{"disambiguationData":[OSD([sQuery(id+"F9.wireOp",EDGE,"E22.rect.bottom"),sQuery(id+"F9.wireOp",EDGE,"E22.rect.left")])]})});
            var Q5;
            Q5=makeQuery(id+"F10.boolean.opBoolean","COPY",EDGE,{"disambiguationData":[OD(1.0)],"derivedFrom":makeQuery(id+"F10.opExtrude","SWEPT_EDGE",EDGE,{"disambiguationData":[OSD([sQuery(id+"F9.wireOp",EDGE,"E22.rect.bottom"),sQuery(id+"F9.wireOp",EDGE,"E22.rect.left")])]})});
            var Q6;
            Q6=makeQuery(id+"F10.boolean.opBoolean","COPY",EDGE,{"disambiguationData":[OD(1.0)],"derivedFrom":makeQuery(id+"F10.opExtrude","SWEPT_EDGE",EDGE,{"disambiguationData":[OSD([sQuery(id+"F9.wireOp",EDGE,"E22.rect.bottom"),sQuery(id+"F9.wireOp",EDGE,"E22.rect.right")])]})});
            var Q7;
            Q7=makeQuery(id+"F10.boolean.opBoolean","COPY",EDGE,{"disambiguationData":[OD(0.0)],"derivedFrom":makeQuery(id+"F10.opExtrude","SWEPT_EDGE",EDGE,{"disambiguationData":[OSD([sQuery(id+"F9.wireOp",EDGE,"E22.rect.bottom"),sQuery(id+"F9.wireOp",EDGE,"E22.rect.right")])]})});
            fillet(context, id + "F19", {"entities" : qUnion([Q0, Q1, Q2, Q3, Q4, Q5, Q6, Q7]), "radius" : 1 * mm, "tangentPropagation" : true, "allowEdgeOverflow" : false});
        }
        {
            var Q0;
            Q0=makeQuery(id+"F4.opExtrude","CAP_EDGE",EDGE,{"disambiguationData":[OSD([sQuery(id+"F2.wireOp",EDGE,"E7")])],"isStart":false});
            var Q1;
            Q1=makeQuery(id+"F4.opExtrude","CAP_EDGE",EDGE,{"disambiguationData":[OSD([sQuery(id+"F2.wireOp",EDGE,"E11.MirrorC")])],"isStart":false});
            fillet(context, id + "F20", {"entities" : qUnion([Q0, Q1]), "radius" : .25 * mm, "tangentPropagation" : true, "allowEdgeOverflow" : false});
        }
        {
            var Q0;
            Q0=qCreatedBy(makeId("Top.planeOp"),FACE);
            var sketch = newSketch(context, id + "F21", { "sketchPlane" : qUnion([Q0])});
            skLineSegment(sketch, "E31", {"start": v(-17.3, 11.57) * mm, "end": v(-13.53, 11.57) * mm});
            skLineSegment(sketch, "E32", {"start": v(-13.53, 11.57) * mm, "end": v(-14.02, 8.59) * mm});
            skLineSegment(sketch, "E33", {"start": v(-14.02, 8.59) * mm, "end": v(-15.95, 8.59) * mm});
            skLineSegment(sketch, "E34", {"start": v(-15.95, 8.59) * mm, "end": v(-17.3, 11.57) * mm});
            skLineSegment(sketch, "E35.MirrorCS", {"start": v(17.3, 11.57) * mm, "end": v(13.53, 11.57) * mm});
            skLineSegment(sketch, "E36.MirrorCS", {"start": v(15.95, 8.59) * mm, "end": v(17.3, 11.57) * mm});
            skLineSegment(sketch, "E37.MirrorCS", {"start": v(14.02, 8.59) * mm, "end": v(15.95, 8.59) * mm});
            skLineSegment(sketch, "E38.MirrorCS", {"start": v(13.53, 11.57) * mm, "end": v(14.02, 8.59) * mm});
            skSolve(sketch);
        }
        {
            var Q0;
            Q0 = qSketchRegion(id + "F21", true);
            extrude(context, id + "F22", {"entities" : qUnion([Q0]), "operationType" : NewBodyOperationType.ADD, "depth" : 34 * mm});
        }
    });
